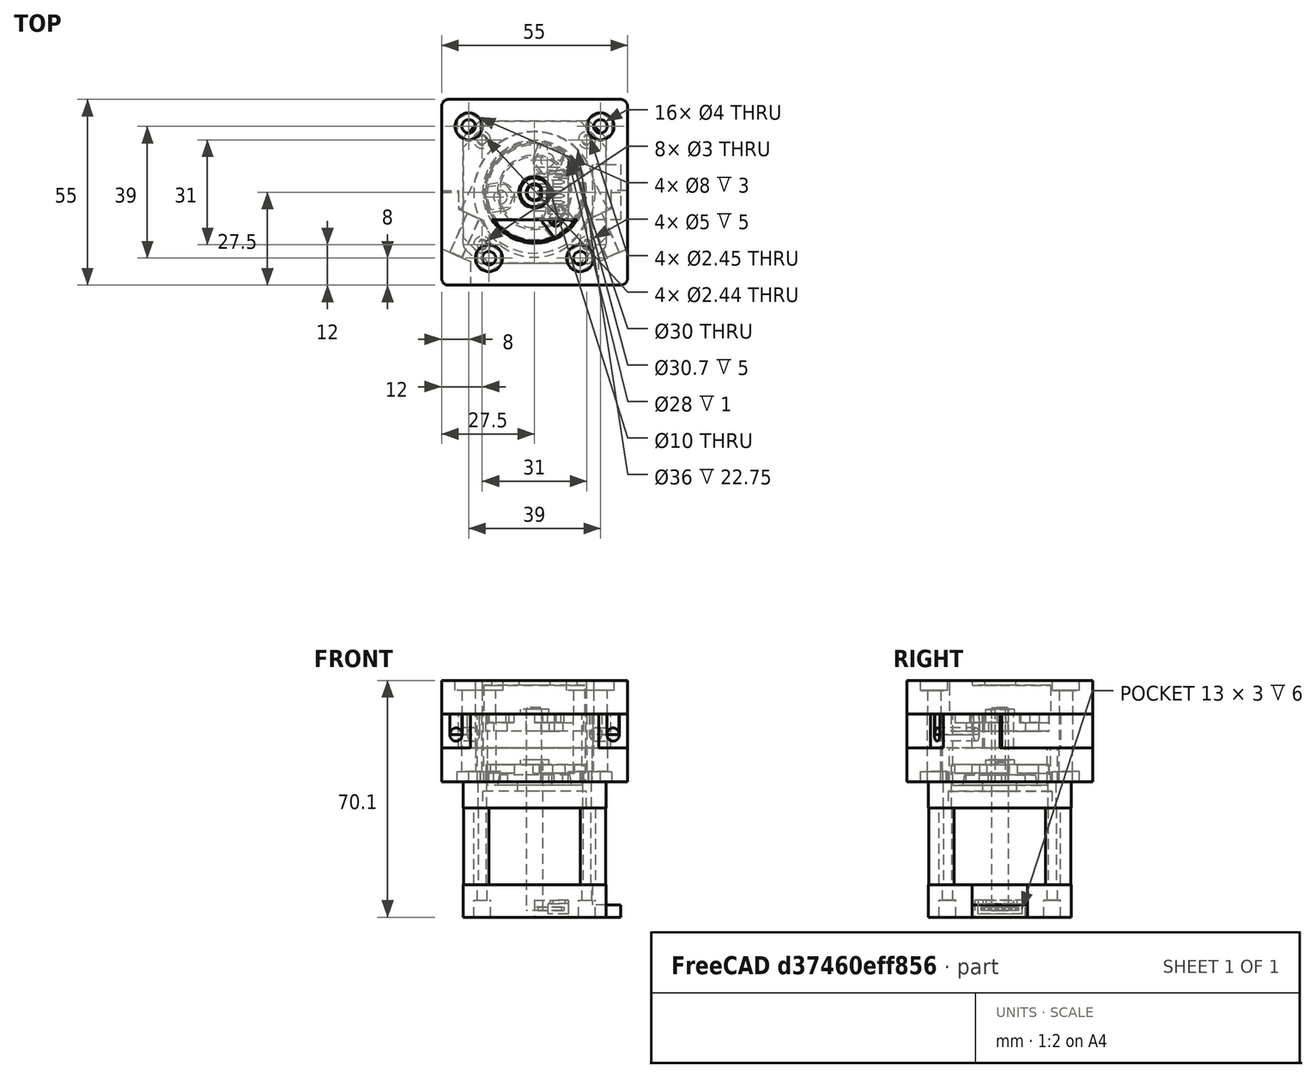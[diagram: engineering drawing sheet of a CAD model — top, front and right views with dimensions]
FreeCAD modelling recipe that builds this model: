
FCSTD DOCUMENT  (FreeCAD 0.19R24291 (Git))
Label: peristaltic-pump
License: All rights reserved
LicenseURL: http://en.wikipedia.org/wiki/All_rights_reserved
objects: Sketcher::SketchObject×44, PartDesign::Pocket×25, PartDesign::Pad×18, PartDesign::Body×12, App::Part×9, Mesh::Feature×5, PartDesign::Chamfer×4, Part::FeaturePython×4, PartDesign::Fillet×2, PartDesign::Mirrored×2, PartDesign::PolarPattern×2, PartDesign::Draft×1, PartDesign::Hole×1, PartDesign::LinearPattern×1, Spreadsheet::Sheet×1, App::MeasureDistance×1
note: 167 computed .brp shape members not serialized (recipe doc carries the construction recipe); baked Part::Feature solids carry a one-line shape summary decoded from their .brp

FEATURE [Sketcher::SketchObject] Sketch
  FullyConstrained = false
  MapMode = 5
  Support = -> [XY_Plane001]
  sketch-geometry (4):
    g0: LineSegment StartX=-21.15 StartY=21.15 StartZ=0 EndX=21.15 EndY=21.15 EndZ=0
    g1: LineSegment StartX=21.15 StartY=21.15 StartZ=0 EndX=21.15 EndY=-21.15 EndZ=0
    g2: LineSegment StartX=21.15 StartY=-21.15 StartZ=0 EndX=-21.15 EndY=-21.15 EndZ=0
    g3: LineSegment StartX=-21.15 StartY=-21.15 StartZ=0 EndX=-21.15 EndY=21.15 EndZ=0
  constraints (11):
    c: Coincident(g0,g1)
    c: Coincident(g1,g2)
    c: Coincident(g2,g3)
    c: Coincident(g3,g0)
    c: Horizontal(g0)
    c: Horizontal(g2)
    c: Vertical(g1)
    c: Vertical(g3)
    c: Symmetric(g0,g1,g-1)
    c: DistanceX(g0,g0) = 42.3
    c: Equal(g0,g3)
FEATURE [PartDesign::Pad] Pad
  AllowMultiFace = false
  Direction = (1,1,1)
  Length = 9.6
  Length2 = 100
  Profile = -> Sketch
  Refine = true
  Type = 0
FEATURE [Sketcher::SketchObject] Sketch001
  ExternalGeometry = -> [Pad]
  FullyConstrained = false
  MapMode = 5
  Support = -> [XY_Plane001]
  sketch-geometry (4):
    g0: LineSegment StartX=21.15 StartY=8.2 StartZ=0 EndX=25.45 EndY=8.2 EndZ=0
    g1: LineSegment StartX=25.45 StartY=8.2 StartZ=0 EndX=25.45 EndY=-8.2 EndZ=0
    g2: LineSegment StartX=25.45 StartY=-8.2 StartZ=0 EndX=21.15 EndY=-8.2 EndZ=0
    g3: LineSegment StartX=21.15 StartY=-8.2 StartZ=0 EndX=21.15 EndY=8.2 EndZ=0
  constraints (11):
    c: Coincident(g0,g1)
    c: Coincident(g1,g2)
    c: Coincident(g2,g3)
    c: Coincident(g3,g0)
    c: Horizontal(g0)
    c: Horizontal(g2)
    c: Vertical(g3)
    c: PointOnObject(g0,g-3)
    c: Symmetric(g1,g0,g-1)
    c: DistanceX(g0,g0) = 4.3
    c: DistanceY(g1,g1) = 16.4
FEATURE [PartDesign::Pad] Pad001
  AllowMultiFace = false
  BaseFeature = -> Pad
  Direction = (1,1,1)
  Length = 3.6
  Length2 = 100
  Profile = -> Sketch001
  Refine = true
  Type = 0
FEATURE [PartDesign::Chamfer] Chamfer
  Angle = 45
  Base = -> Pad001 [Edge13,Edge5,Edge1,Edge2]
  BaseFeature = -> Pad001
  ChamferType = 0
  FlipDirection = false
  Size = 5
  Size2 = 1
  SupportTransform = false
FEATURE [PartDesign::Fillet] Fillet
  Base = -> Chamfer [Edge33,Edge28,Edge18,Edge3,Edge2,Edge16,Edge30,Edge25]
  BaseFeature = -> Chamfer
  Radius = 2
  SupportTransform = false
FEATURE [Sketcher::SketchObject] Sketch002
  FullyConstrained = false
  MapMode = 5
  Support = -> [XY_Plane002]
  sketch-geometry (4):
    g0: LineSegment StartX=-21 StartY=21 StartZ=0 EndX=21 EndY=21 EndZ=0
    g1: LineSegment StartX=21 StartY=21 StartZ=0 EndX=21 EndY=-21 EndZ=0
    g2: LineSegment StartX=21 StartY=-21 StartZ=0 EndX=-21 EndY=-21 EndZ=0
    g3: LineSegment StartX=-21 StartY=-21 StartZ=0 EndX=-21 EndY=21 EndZ=0
  constraints (11):
    c: Coincident(g0,g1)
    c: Coincident(g1,g2)
    c: Coincident(g2,g3)
    c: Coincident(g3,g0)
    c: Horizontal(g0)
    c: Horizontal(g2)
    c: Vertical(g1)
    c: Vertical(g3)
    c: DistanceX(g0,g0) = 42
    c: Symmetric(g0,g1,g-1)
    c: Equal(g0,g3)
FEATURE [PartDesign::Pad] Pad002
  AllowMultiFace = false
  Direction = (1,1,1)
  Length = 22.75
  Length2 = 100
  Profile = -> Sketch002
  Refine = true
  Type = 0
FEATURE [PartDesign::Chamfer] Chamfer001
  Angle = 45
  Base = -> Pad002 [Edge8,Edge1,Edge5,Edge2]
  BaseFeature = -> Pad002
  ChamferType = 0
  FlipDirection = false
  Size = 7.5
  Size2 = 1
  SupportTransform = false
FEATURE [Sketcher::SketchObject] Sketch003
  FullyConstrained = false
  MapMode = 5
  Support = -> [XY_Plane003]
  sketch-geometry (4):
    g0: LineSegment StartX=-21.15 StartY=21.15 StartZ=0 EndX=21.15 EndY=21.15 EndZ=0
    g1: LineSegment StartX=21.15 StartY=21.15 StartZ=0 EndX=21.15 EndY=-21.15 EndZ=0
    g2: LineSegment StartX=21.15 StartY=-21.15 StartZ=0 EndX=-21.15 EndY=-21.15 EndZ=0
    g3: LineSegment StartX=-21.15 StartY=-21.15 StartZ=0 EndX=-21.15 EndY=21.15 EndZ=0
  constraints (11):
    c: Coincident(g0,g1)
    c: Coincident(g1,g2)
    c: Coincident(g2,g3)
    c: Coincident(g3,g0)
    c: Horizontal(g0)
    c: Horizontal(g2)
    c: Vertical(g1)
    c: Vertical(g3)
    c: Symmetric(g0,g1,g-1)
    c: DistanceX(g0,g0) = 42.3
    c: Equal(g0,g3)
FEATURE [PartDesign::Pad] Pad003
  AllowMultiFace = false
  Direction = (1,1,1)
  Length = 7.75
  Length2 = 100
  Profile = -> Sketch003
  Refine = true
  Type = 0
FEATURE [PartDesign::Chamfer] Chamfer002
  Angle = 45
  Base = -> Pad003 [Edge8,Edge5,Edge2,Edge1]
  BaseFeature = -> Pad003
  ChamferType = 0
  FlipDirection = false
  Size = 5
  Size2 = 1
  SupportTransform = false
FEATURE [PartDesign::Fillet] Fillet001
  Base = -> Chamfer002 [Edge22,Edge24,Edge23,Edge21,Edge12,Edge2,Edge3,Edge14]
  BaseFeature = -> Chamfer002
  Radius = 2
  SupportTransform = false
FEATURE [Sketcher::SketchObject] Sketch004
  FullyConstrained = false
  MapMode = 5
  Placement = pos=(0,0,0) rot=(1,0,0;3.14159rad)
  Support = -> [Fillet]
  sketch-geometry (8):
    g0: LineSegment StartX=-15.5 StartY=15.5 StartZ=0 EndX=15.5 EndY=15.5 EndZ=0
    g1: LineSegment StartX=15.5 StartY=15.5 StartZ=0 EndX=15.5 EndY=-15.5 EndZ=0
    g2: LineSegment StartX=15.5 StartY=-15.5 StartZ=0 EndX=-15.5 EndY=-15.5 EndZ=0
    g3: LineSegment StartX=-15.5 StartY=-15.5 StartZ=0 EndX=-15.5 EndY=15.5 EndZ=0
    g4: Circle CenterX=-15.5 CenterY=15.5 CenterZ=0 NormalX=0 NormalY=0 NormalZ=1 AngleXU=0 Radius=1.225
    g5: Circle CenterX=15.5 CenterY=15.5 CenterZ=0 NormalX=0 NormalY=0 NormalZ=1 AngleXU=0 Radius=1.225
    g6: Circle CenterX=15.5 CenterY=-15.5 CenterZ=0 NormalX=0 NormalY=0 NormalZ=1 AngleXU=0 Radius=1.225
    g7: Circle CenterX=-15.5 CenterY=-15.5 CenterZ=0 NormalX=0 NormalY=0 NormalZ=1 AngleXU=0 Radius=1.225
  constraints (19):
    c: Coincident(g0,g1)
    c: Coincident(g1,g2)
    c: Coincident(g2,g3)
    c: Coincident(g3,g0)
    c: Horizontal(g0)
    c: Horizontal(g2)
    c: Vertical(g1)
    c: Vertical(g3)
    c: Symmetric(g0,g1,g-1)
    c: DistanceX(g0,g0) = 31
    c: Equal(g3,g0)
    c: Coincident(g4,g0)
    c: Coincident(g5,g0)
    c: Coincident(g6,g1)
    c: Coincident(g7,g2)
    c: Equal(g6,g5)
    c: Equal(g5,g4)
    c: Equal(g4,g7)
    c: Radius(g4) = 1.225
FEATURE [Sketcher::SketchObject] Sketch005
  FullyConstrained = false
  MapMode = 5
  Placement = pos=(0,0,0) rot=(1,0,0;3.14159rad)
  Support = -> [Chamfer001]
  sketch-geometry (8):
    g0: LineSegment StartX=-15.5 StartY=15.5 StartZ=0 EndX=15.5 EndY=15.5 EndZ=0
    g1: LineSegment StartX=15.5 StartY=15.5 StartZ=0 EndX=15.5 EndY=-15.5 EndZ=0
    g2: LineSegment StartX=15.5 StartY=-15.5 StartZ=0 EndX=-15.5 EndY=-15.5 EndZ=0
    g3: LineSegment StartX=-15.5 StartY=-15.5 StartZ=0 EndX=-15.5 EndY=15.5 EndZ=0
    g4: Circle CenterX=-15.5 CenterY=15.5 CenterZ=0 NormalX=0 NormalY=0 NormalZ=1 AngleXU=0 Radius=1.22
    g5: Circle CenterX=15.5 CenterY=15.5 CenterZ=0 NormalX=0 NormalY=0 NormalZ=1 AngleXU=0 Radius=1.22
    g6: Circle CenterX=15.5 CenterY=-15.5 CenterZ=0 NormalX=0 NormalY=0 NormalZ=1 AngleXU=0 Radius=1.22
    g7: Circle CenterX=-15.5 CenterY=-15.5 CenterZ=0 NormalX=0 NormalY=0 NormalZ=1 AngleXU=0 Radius=1.22
  constraints (19):
    c: Coincident(g0,g1)
    c: Coincident(g1,g2)
    c: Coincident(g2,g3)
    c: Coincident(g3,g0)
    c: Horizontal(g0)
    c: Horizontal(g2)
    c: Vertical(g1)
    c: Vertical(g3)
    c: Equal(g0,g3)
    c: Symmetric(g0,g1,g-1)
    c: DistanceX(g0,g0) = 31
    c: Coincident(g4,g0)
    c: Coincident(g5,g0)
    c: Coincident(g6,g1)
    c: Coincident(g7,g2)
    c: Equal(g6,g5)
    c: Equal(g5,g4)
    c: Equal(g4,g7)
    c: Radius(g4) = 1.22
FEATURE [PartDesign::Pocket] Pocket001
  AllowMultiFace = false
  BaseFeature = -> Chamfer001
  Length = 5
  Length2 = 100
  Profile = -> Sketch005
  Refine = true
  Type = 1
FEATURE [Sketcher::SketchObject] Sketch010
  FullyConstrained = false
  MapMode = 5
  Support = -> [XY_Plane004]
  sketch-geometry (1):
    g0: Circle CenterX=0 CenterY=0 CenterZ=0 NormalX=0 NormalY=0 NormalZ=1 AngleXU=0 Radius=2.5
  constraints (2):
    c: Coincident(g0,g-1)
    c: Radius(g0) = 2.5
FEATURE [PartDesign::Pad] Pad005
  AllowMultiFace = false
  Direction = (1,1,1)
  Length = 60
  Length2 = 100
  Profile = -> Sketch010
  Refine = true
  Type = 0
FEATURE [Sketcher::SketchObject] Sketch011
  FullyConstrained = false
  MapMode = 5
  Placement = pos=(0,0,60) rot=(0,0,1;0rad)
  Support = -> [Pad005]
  sketch-geometry (4):
    g0: LineSegment StartX=2 StartY=2 StartZ=0 EndX=6 EndY=2 EndZ=0
    g1: LineSegment StartX=6 StartY=2 StartZ=0 EndX=6 EndY=-2 EndZ=0
    g2: LineSegment StartX=6 StartY=-2 StartZ=0 EndX=2 EndY=-2 EndZ=0
    g3: LineSegment StartX=2 StartY=-2 StartZ=0 EndX=2 EndY=2 EndZ=0
  constraints (11):
    c: Coincident(g0,g1)
    c: Coincident(g1,g2)
    c: Coincident(g2,g3)
    c: Coincident(g3,g0)
    c: Horizontal(g0)
    c: Horizontal(g2)
    c: Vertical(g1)
    c: Symmetric(g2,g0,g-1)
    c: DistanceX(g-1,g0) = 2
    c: Equal(g0,g3)
    c: DistanceX(g0,g0) = 4
FEATURE [PartDesign::Pocket] Pocket005
  AllowMultiFace = false
  BaseFeature = -> Pad005
  Length = 16
  Length2 = 100
  Profile = -> Sketch011
  Refine = true
  Type = 0
FEATURE [PartDesign::Chamfer] Chamfer003
  Angle = 45
  Base = -> Pocket005 [Edge3,Edge5,Edge9]
  BaseFeature = -> Pocket005
  ChamferType = 0
  FlipDirection = false
  Size = 0.3
  Size2 = 1
  SupportTransform = false
FEATURE [PartDesign::Body] Body003  label="Rotor"
  Group = -> [Sketch010,Pad005,Sketch011,Pocket005,Chamfer003]
  Origin = -> Origin004
  Placement = pos=(0,0,2) rot=(0,0,1;0rad)
  Tip = -> Chamfer003
FEATURE [Sketcher::SketchObject] Sketch012
  FullyConstrained = false
  MapMode = 5
  Placement = pos=(0,0,22.75) rot=(0,0,1;0rad)
  Support = -> [Pocket001]
  sketch-geometry (1):
    g0: Circle CenterX=0 CenterY=0 CenterZ=0 NormalX=0 NormalY=0 NormalZ=1 AngleXU=0 Radius=18
  constraints (2):
    c: Coincident(g0,g-1)
    c: Radius(g0) = 18
FEATURE [Sketcher::SketchObject] Sketch006
  FullyConstrained = false
  MapMode = 5
  Placement = pos=(0,0,7.75) rot=(0,0,1;0rad)
  Support = -> [Fillet001]
  sketch-geometry (8):
    g0: LineSegment StartX=-15.5 StartY=15.5 StartZ=0 EndX=15.5 EndY=15.5 EndZ=0
    g1: LineSegment StartX=15.5 StartY=15.5 StartZ=0 EndX=15.5 EndY=-15.5 EndZ=0
    g2: LineSegment StartX=15.5 StartY=-15.5 StartZ=0 EndX=-15.5 EndY=-15.5 EndZ=0
    g3: LineSegment StartX=-15.5 StartY=-15.5 StartZ=0 EndX=-15.5 EndY=15.5 EndZ=0
    g4: Circle CenterX=-15.5 CenterY=15.5 CenterZ=0 NormalX=0 NormalY=0 NormalZ=1 AngleXU=0 Radius=1.225
    g5: Circle CenterX=15.5 CenterY=15.5 CenterZ=0 NormalX=0 NormalY=0 NormalZ=1 AngleXU=0 Radius=1.225
    g6: Circle CenterX=15.5 CenterY=-15.5 CenterZ=0 NormalX=0 NormalY=0 NormalZ=1 AngleXU=0 Radius=1.225
    g7: Circle CenterX=-15.5 CenterY=-15.5 CenterZ=0 NormalX=0 NormalY=0 NormalZ=1 AngleXU=0 Radius=1.225
  constraints (19):
    c: Coincident(g0,g1)
    c: Coincident(g1,g2)
    c: Coincident(g2,g3)
    c: Coincident(g3,g0)
    c: Horizontal(g0)
    c: Horizontal(g2)
    c: Vertical(g1)
    c: Vertical(g3)
    c: Equal(g0,g3)
    c: Symmetric(g0,g1,g-1)
    c: DistanceX(g0,g0) = 31
    c: Coincident(g4,g0)
    c: Coincident(g7,g2)
    c: Coincident(g0,g5)
    c: Coincident(g1,g6)
    c: Equal(g7,g4)
    c: Equal(g4,g5)
    c: Equal(g5,g6)
    c: Radius(g4) = 1.225
FEATURE [PartDesign::Pocket] Pocket002
  AllowMultiFace = false
  BaseFeature = -> Fillet001
  Length = 5
  Length2 = 100
  Profile = -> Sketch006
  Refine = true
  Type = 1
FEATURE [Sketcher::SketchObject] Sketch007
  FullyConstrained = false
  MapMode = 5
  Placement = pos=(0,0,7.75) rot=(0,0,1;0rad)
  Support = -> [Pocket002]
  sketch-geometry (1):
    g0: Circle CenterX=0 CenterY=0 CenterZ=0 NormalX=0 NormalY=0 NormalZ=1 AngleXU=0 Radius=14
  constraints (2):
    c: Coincident(g0,g-1)
    c: Radius(g0) = 14
FEATURE [PartDesign::Pocket] Pocket003
  AllowMultiFace = false
  BaseFeature = -> Pocket002
  Length = 1
  Length2 = 100
  Profile = -> Sketch007
  Refine = true
  Type = 0
FEATURE [Sketcher::SketchObject] Sketch008
  FullyConstrained = false
  MapMode = 5
  Placement = pos=(0,0,6.75) rot=(0,0,1;0rad)
  Support = -> [Pocket003]
  sketch-geometry (1):
    g0: Circle CenterX=0 CenterY=0 CenterZ=0 NormalX=0 NormalY=0 NormalZ=1 AngleXU=0 Radius=11
  constraints (2):
    c: Coincident(g0,g-1)
    c: Radius(g0) = 11
FEATURE [PartDesign::Pad] Pad004
  AllowMultiFace = false
  BaseFeature = -> Pocket003
  Direction = (1,1,1)
  Length = 3
  Length2 = 100
  Profile = -> Sketch008
  Refine = true
  Type = 0
FEATURE [PartDesign::Draft] Draft
  Angle = 10
  Base = -> Pad004 [Face25]
  BaseFeature = -> Pad004
  NeutralPlane = -> Pad004 [Face24]
  SupportTransform = false
FEATURE [Sketcher::SketchObject] Sketch009
  FullyConstrained = false
  MapMode = 5
  Placement = pos=(0,0,9.75) rot=(0,0,1;0rad)
  Support = -> [Draft]
  sketch-geometry (1):
    g0: Circle CenterX=0 CenterY=0 CenterZ=0 NormalX=0 NormalY=0 NormalZ=1 AngleXU=0 Radius=5
  constraints (2):
    c: Coincident(g0,g-1)
    c: Radius(g0) = 5
FEATURE [PartDesign::Pocket] Pocket004
  AllowMultiFace = false
  BaseFeature = -> Draft
  Length = 8
  Length2 = 100
  Profile = -> Sketch009
  Refine = true
  Type = 1
FEATURE [PartDesign::Hole] Hole
  AllowMultiFace = false
  BaseFeature = -> Fillet
  Depth = 25
  DepthType = 0
  Diameter = 3
  DrillForDepth = false
  DrillPoint = 1
  DrillPointAngle = 118
  HoleCutCountersinkAngle = 90
  HoleCutCustomValues = false
  HoleCutDepth = 5
  HoleCutDiameter = 5
  HoleCutType = 1
  ModelActualThread = false
  Profile = -> Sketch004
  Refine = true
  Tapered = false
  TaperedAngle = 90
  ThreadAngle = 0
  ThreadClass = 0
  ThreadCutOffInner = 0
  ThreadCutOffOuter = 0
  ThreadDirection = 0
  ThreadFit = 0
  ThreadPitch = 0
  ThreadSize = 0
  ThreadType = 0
  Threaded = false
FEATURE [Part::FeaturePython] Screw  label="M2.5x25-Screw"  # Fasteners workbench fastener (typed FeaturePython)
  Placement = pos=(15.5,15.5,4) rot=(0,1,0;3.14159rad)
  diameter = 3
  invert = true
  length = 10
  matchOuter = true
  offset = 1
  thread = true
  type = 16
FEATURE [Part::FeaturePython] Screw001  label="M2.5x25-Screw006"  # Fasteners workbench fastener (typed FeaturePython)
  Placement = pos=(-15.5,-15.5,4) rot=(0,1,0;3.14159rad)
  diameter = 3
  invert = true
  length = 10
  matchOuter = true
  offset = 1
  thread = true
  type = 16
FEATURE [Part::FeaturePython] Screw002  label="M2.5x25-Screw005"  # Fasteners workbench fastener (typed FeaturePython)
  Placement = pos=(15.5,-15.5,4) rot=(0,1,0;3.14159rad)
  diameter = 3
  invert = true
  length = 10
  matchOuter = true
  offset = 1
  thread = true
  type = 16
FEATURE [Part::FeaturePython] Screw003  label="M2.5x25-Screw007"  # Fasteners workbench fastener (typed FeaturePython)
  Placement = pos=(-15.5,15.5,4) rot=(0,1,0;3.14159rad)
  diameter = 3
  invert = true
  length = 10
  matchOuter = true
  offset = 1
  thread = true
  type = 16
FEATURE [App::Part] Part004  label="Rotor001"
  Group = -> [Body003]
  Origin = -> Origin008
FEATURE [App::Part] Part005  label="Screw"
  Group = -> [Screw,Screw001,Screw002,Screw003]
  Origin = -> Origin009
FEATURE [PartDesign::Body] Body004  label="Stator"
  Origin = -> Origin010
FEATURE [PartDesign::Pocket] Pocket
  AllowMultiFace = false
  BaseFeature = -> Pocket001
  Length = 5
  Length2 = 100
  Profile = -> Sketch012
  Refine = true
  Type = 1
FEATURE [PartDesign::Body] Body001
  Group = -> [Sketch002,Pad002,Chamfer001,Sketch005,Pocket001,Sketch012,Pocket]
  Origin = -> Origin002
  Placement = pos=(0,0,9.6) rot=(0,0,1;0rad)
  Tip = -> Pocket
FEATURE [App::Part] Part002  label="Body"
  Group = -> [Body001,Body004]
  Origin = -> Origin006
FEATURE [Sketcher::SketchObject] Sketch013
  ExternalGeometry = -> [Hole]
  FullyConstrained = false
  MapMode = 5
  Placement = pos=(21.15,0,0) rot=(0.57735,0.57735,0.57735;2.0944rad)
  Support = -> [Hole]
  sketch-geometry (4):
    g0: LineSegment StartX=-8.2 StartY=3.6 StartZ=0 EndX=8.2 EndY=3.6 EndZ=0
    g1: LineSegment StartX=8.2 StartY=3.6 StartZ=0 EndX=8.2 EndY=9.6 EndZ=0
    g2: LineSegment StartX=8.2 StartY=9.6 StartZ=0 EndX=-8.2 EndY=9.6 EndZ=0
    g3: LineSegment StartX=-8.2 StartY=9.6 StartZ=0 EndX=-8.2 EndY=3.6 EndZ=0
  constraints (10):
    c: Coincident(g0,g1)
    c: Coincident(g1,g2)
    c: Coincident(g2,g3)
    c: Coincident(g3,g0)
    c: Horizontal(g0)
    c: Vertical(g1)
    c: Vertical(g3)
    c: Coincident(g0,g-3)
    c: PointOnObject(g1,g-5)
    c: Symmetric(g2,g1,g-2)
FEATURE [PartDesign::Pocket] Pocket006
  AllowMultiFace = false
  BaseFeature = -> Hole
  Length = 4
  Length2 = 100
  Profile = -> Sketch013
  Refine = true
  Type = 0
FEATURE [PartDesign::Body] Body  label="Aluminium rear001"
  Group = -> [Sketch,Pad,Sketch001,Pad001,Chamfer,Fillet,Sketch004,Hole,Sketch013,Pocket006]
  Origin = -> Origin001
  Tip = -> Pocket006
FEATURE [App::Part] Part001  label="Aluminium rear"
  Group = -> [Body]
  Origin = -> Origin005
FEATURE [Sketcher::SketchObject] Sketch014
  FullyConstrained = false
  MapMode = 5
  Placement = pos=(0,0,0) rot=(0.57735,0.57735,0.57735;2.0944rad)
  Support = -> [YZ_Plane012]
  sketch-geometry (4):
    g0: LineSegment StartX=-7.5 StartY=0 StartZ=0 EndX=7.5 EndY=0 EndZ=0
    g1: LineSegment StartX=7.5 StartY=0 StartZ=0 EndX=7.5 EndY=5 EndZ=0
    g2: LineSegment StartX=7.5 StartY=5 StartZ=0 EndX=-7.5 EndY=5 EndZ=0
    g3: LineSegment StartX=-7.5 StartY=5 StartZ=0 EndX=-7.5 EndY=0 EndZ=0
  constraints (11):
    c: Coincident(g0,g1)
    c: Coincident(g1,g2)
    c: Coincident(g2,g3)
    c: Coincident(g3,g0)
    c: Horizontal(g0)
    c: Horizontal(g2)
    c: Vertical(g1)
    c: Vertical(g3)
    c: Symmetric(g0,g0,g-1)
    c: DistanceX(g0,g0) = 15
    c: DistanceY(g3,g3) = 5
FEATURE [PartDesign::Pad] Pad006
  AllowMultiFace = false
  Direction = (1,1,1)
  Length = 10
  Length2 = 100
  Placement = pos=(0,0,0) rot=(0.57735,0.57735,0.57735;2.0944rad)
  Profile = -> Sketch014
  Refine = true
  Type = 0
FEATURE [Sketcher::SketchObject] Sketch015
  ExternalGeometry = -> [Pad006]
  FullyConstrained = false
  MapMode = 5
  Placement = pos=(10,-2.2e-15,2.2e-15) rot=(0.57735,0.57735,0.57735;2.0944rad)
  Support = -> [Pad006]
  sketch-geometry (8):
    g0: LineSegment StartX=-6.5 StartY=4 StartZ=0 EndX=6.5 EndY=4 EndZ=0
    g1: LineSegment StartX=6.5 StartY=4 StartZ=0 EndX=6.5 EndY=1 EndZ=0
    g2: LineSegment StartX=6.5 StartY=1 StartZ=0 EndX=-6.5 EndY=1 EndZ=0
    g3: LineSegment StartX=-6.5 StartY=1 StartZ=0 EndX=-6.5 EndY=4 EndZ=0
    g4: LineSegment StartX=-6.5 StartY=1 StartZ=0 EndX=-7.5 EndY=1 EndZ=0
    g5: LineSegment StartX=-6.5 StartY=1 StartZ=0 EndX=-6.5 EndY=0 EndZ=0
    g6: LineSegment StartX=6.5 StartY=4 StartZ=0 EndX=6.5 EndY=5 EndZ=0
    g7: LineSegment StartX=6.5 StartY=4 StartZ=0 EndX=7.5 EndY=4 EndZ=0
  constraints (23):
    c: Coincident(g0,g1)
    c: Coincident(g1,g2)
    c: Coincident(g2,g3)
    c: Coincident(g3,g0)
    c: Horizontal(g2)
    c: Vertical(g1)
    c: Vertical(g3)
    c: Symmetric(g0,g0,g-2)
    c: Coincident(g4,g2)
    c: PointOnObject(g4,g-4)
    c: Horizontal(g4)
    c: PointOnObject(g5,g-1)
    c: Vertical(g5)
    c: Coincident(g6,g0)
    c: Coincident(g7,g0)
    c: Horizontal(g7)
    c: Vertical(g6)
    c: PointOnObject(g6,g-5)
    c: Equal(g7,g6)
    c: Equal(g6,g4)
    c: Equal(g4,g5)
    c: DistanceX(g4,g4) = 1
    c: Coincident(g5,g2)
FEATURE [PartDesign::Pocket] Pocket007
  AllowMultiFace = false
  BaseFeature = -> Pad006
  Length = 6
  Length2 = 100
  Placement = pos=(0,0,0) rot=(0.57735,0.57735,0.57735;2.0944rad)
  Profile = -> Sketch015
  Refine = true
  Type = 0
FEATURE [Sketcher::SketchObject] Sketch016
  ExternalGeometry = -> [Pocket007]
  FullyConstrained = false
  MapMode = 5
  Placement = pos=(10,-2.2e-15,2.2e-15) rot=(0.57735,0.57735,0.57735;2.0944rad)
  Support = -> [Pocket007]
  sketch-geometry (4):
    g0: LineSegment StartX=-4 StartY=5 StartZ=0 EndX=4 EndY=5 EndZ=0
    g1: LineSegment StartX=4 StartY=5 StartZ=0 EndX=4 EndY=4 EndZ=0
    g2: LineSegment StartX=4 StartY=4 StartZ=0 EndX=-4 EndY=4 EndZ=0
    g3: LineSegment StartX=-4 StartY=4 StartZ=0 EndX=-4 EndY=5 EndZ=0
  constraints (11):
    c: Coincident(g0,g1)
    c: Coincident(g1,g2)
    c: Coincident(g2,g3)
    c: Coincident(g3,g0)
    c: Horizontal(g0)
    c: Vertical(g1)
    c: Vertical(g3)
    c: PointOnObject(g0,g-3)
    c: PointOnObject(g1,g-4)
    c: Symmetric(g1,g2,g-2)
    c: DistanceX(g0,g0) = 8
FEATURE [PartDesign::Pocket] Pocket008
  AllowMultiFace = false
  BaseFeature = -> Pocket007
  Length = 4.5
  Length2 = 100
  Placement = pos=(0,0,0) rot=(0.57735,0.57735,0.57735;2.0944rad)
  Profile = -> Sketch016
  Refine = true
  Type = 0
FEATURE [Sketcher::SketchObject] Sketch017
  ExternalGeometry = -> [Pocket008]
  FullyConstrained = false
  MapMode = 5
  Placement = pos=(-1.4e-15,2.2e-15,5) rot=(0,0,-1;1.5708rad)
  Support = -> [Pocket008]
  sketch-geometry (11):
    g0: LineSegment StartX=-6.49 StartY=8.99 StartZ=0 EndX=-5.01 EndY=8.99 EndZ=0
    g1: LineSegment StartX=-5.01 StartY=8.99 StartZ=0 EndX=-5.01 EndY=4.5 EndZ=0
    g2: LineSegment StartX=-5.01 StartY=4.5 StartZ=0 EndX=-6.49 EndY=4.5 EndZ=0
    g3: LineSegment StartX=-6.49 StartY=4.5 StartZ=0 EndX=-6.49 EndY=8.99 EndZ=0
    g4: LineSegment StartX=5.01 StartY=8.99 StartZ=0 EndX=6.49 EndY=8.99 EndZ=0
    g5: LineSegment StartX=6.49 StartY=8.99 StartZ=0 EndX=6.49 EndY=4.5 EndZ=0
    g6: LineSegment StartX=6.49 StartY=4.5 StartZ=0 EndX=5.01 EndY=4.5 EndZ=0
    g7: LineSegment StartX=5.01 StartY=4.5 StartZ=0 EndX=5.01 EndY=8.99 EndZ=0
    g8: LineSegment StartX=-7.5 StartY=8.99 StartZ=0 EndX=-6.49 EndY=8.99 EndZ=0
    g9: LineSegment StartX=-6.49 StartY=10 StartZ=0 EndX=-6.49 EndY=8.99 EndZ=0
    g10: LineSegment StartX=-5.01 StartY=8.99 StartZ=0 EndX=-4 EndY=8.99 EndZ=0
  constraints (32):
    c: Coincident(g0,g1)
    c: Coincident(g1,g2)
    c: Coincident(g2,g3)
    c: Coincident(g3,g0)
    c: Horizontal(g0)
    c: Horizontal(g2)
    c: Vertical(g1)
    c: Vertical(g3)
    c: Coincident(g4,g5)
    c: Coincident(g5,g6)
    c: Coincident(g6,g7)
    c: Coincident(g7,g4)
    c: Horizontal(g4)
    c: Horizontal(g6)
    c: Vertical(g5)
    c: Vertical(g7)
    c: DistanceX(g4,g4) = 1.48
    c: Equal(g0,g4)
    c: Equal(g7,g1)
    c: PointOnObject(g8,g-4)
    c: Coincident(g8,g0)
    c: Horizontal(g8)
    c: PointOnObject(g9,g-5)
    c: Coincident(g9,g0)
    c: Vertical(g9)
    c: Coincident(g10,g0)
    c: PointOnObject(g10,g-3)
    c: Horizontal(g10)
    c: Symmetric(g4,g0,g-2)
    c: Equal(g10,g9)
    c: Equal(g9,g8)
    c: DistanceY(g3,g3) = 4.49
FEATURE [PartDesign::Pocket] Pocket009
  AllowMultiFace = false
  BaseFeature = -> Pocket008
  Length = 2
  Length2 = 100
  Placement = pos=(0,0,0) rot=(0.57735,0.57735,0.57735;2.0944rad)
  Profile = -> Sketch017
  Refine = true
  Type = 0
FEATURE [PartDesign::Body] Body005  label="conector"
  Group = -> [Sketch014,Pad006,Sketch015,Pocket007,Sketch016,Pocket008,Sketch017,Pocket009]
  Origin = -> Origin012
  Tip = -> Pocket009
FEATURE [Sketcher::SketchObject] Sketch018
  FullyConstrained = false
  MapMode = 5
  Placement = pos=(0,0,0) rot=(0.57735,0.57735,0.57735;2.0944rad)
  Support = -> [YZ_Plane013]
  sketch-geometry (4):
    g0: LineSegment StartX=-5.5 StartY=1 StartZ=0 EndX=5.5 EndY=1 EndZ=0
    g1: LineSegment StartX=5.5 StartY=1 StartZ=0 EndX=5.5 EndY=0 EndZ=0
    g2: LineSegment StartX=5.5 StartY=0 StartZ=0 EndX=-5.5 EndY=0 EndZ=0
    g3: LineSegment StartX=-5.5 StartY=0 StartZ=0 EndX=-5.5 EndY=1 EndZ=0
  constraints (11):
    c: Coincident(g0,g1)
    c: Coincident(g1,g2)
    c: Coincident(g2,g3)
    c: Coincident(g3,g0)
    c: Horizontal(g0)
    c: Vertical(g1)
    c: Vertical(g3)
    c: PointOnObject(g1,g-1)
    c: DistanceY(g3,g3) = 1
    c: DistanceX(g2,g2) = 11
    c: Symmetric(g1,g2,g-2)
FEATURE [PartDesign::Pad] Pad007
  AllowMultiFace = false
  Direction = (1,1,1)
  Length = 1
  Length2 = 100
  Placement = pos=(0,0,0) rot=(0.57735,0.57735,0.57735;2.0944rad)
  Profile = -> Sketch018
  Refine = true
  Type = 0
FEATURE [Sketcher::SketchObject] Sketch019
  ExternalGeometry = -> [Pad007]
  FullyConstrained = false
  MapMode = 5
  Placement = pos=(-3e-16,4e-16,1) rot=(0,0,-1;1.5708rad)
  Support = -> [Pad007]
  sketch-geometry (7):
    g0: LineSegment StartX=-5.5 StartY=1 StartZ=0 EndX=-4.5 EndY=1 EndZ=0
    g1: LineSegment StartX=-4.5 StartY=1 StartZ=0 EndX=-4.5 EndY=8 EndZ=0
    g2: LineSegment StartX=-4.5 StartY=8 StartZ=0 EndX=-5.5 EndY=8 EndZ=0
    g3: LineSegment StartX=-5.5 StartY=8 StartZ=0 EndX=-5.5 EndY=1 EndZ=0
    g4: LineSegment StartX=-5.5 StartY=8 StartZ=0 EndX=-5.25 EndY=8.7 EndZ=0
    g5: LineSegment StartX=-5.25 StartY=8.7 StartZ=0 EndX=-4.75 EndY=8.7 EndZ=0
    g6: LineSegment StartX=-4.75 StartY=8.7 StartZ=0 EndX=-4.5 EndY=8 EndZ=0
  constraints (19):
    c: Coincident(g0,g1)
    c: Coincident(g1,g2)
    c: Coincident(g2,g3)
    c: Coincident(g3,g0)
    c: Horizontal(g0)
    c: Horizontal(g2)
    c: Vertical(g1)
    c: Vertical(g3)
    c: Coincident(g0,g-3)
    c: Coincident(g2,g4)
    c: Coincident(g4,g5)
    c: Horizontal(g5)
    c: Coincident(g5,g6)
    c: Coincident(g6,g1)
    c: DistanceY(g1,g5) = 0.7
    c: DistanceX(g5,g5) = 0.5
    c: Equal(g6,g4)
    c: DistanceX(g0,g0) = 1
    c: DistanceY(g3,g3) = 7
FEATURE [PartDesign::Pad] Pad008
  AllowMultiFace = false
  BaseFeature = -> Pad007
  Direction = (1,1,1)
  Length = 1
  Length2 = 100
  Placement = pos=(0,0,0) rot=(0.57735,0.57735,0.57735;2.0944rad)
  Profile = -> Sketch019
  Refine = true
  Reversed = true
  Type = 0
FEATURE [PartDesign::LinearPattern] LinearPattern
  BaseFeature = -> Pad008
  Direction = -> Pad008 [Edge10]
  Length = 10
  Occurrences = 6
  Originals = -> [Pad008]
  Placement = pos=(0,0,0) rot=(0.57735,0.57735,0.57735;2.0944rad)
  Refine = true
  Reversed = true
FEATURE [PartDesign::Body] Body006  label="pin"
  Group = -> [Sketch018,Pad007,Sketch019,Pad008,LinearPattern]
  Origin = -> Origin013
  Placement = pos=(0,0,2) rot=(0,0,1;0rad)
  Tip = -> LinearPattern
FEATURE [App::Part] Part006  label="Conector"
  Group = -> [Body005,Body006]
  Origin = -> Origin011
  Placement = pos=(17,0,4) rot=(0,0,1;0rad)
FEATURE [Sketcher::SketchObject] Sketch020
  FullyConstrained = false
  MapMode = 5
  Placement = pos=(0,0,0) rot=(1,0,0;3.14159rad)
  Support = -> [Pocket004]
  sketch-geometry (1):
    g0: Circle CenterX=0 CenterY=0 CenterZ=0 NormalX=0 NormalY=0 NormalZ=1 AngleXU=0 Radius=15.35
  constraints (2):
    c: Coincident(g0,g-1)
    c: Radius(g0) = 15.35
FEATURE [PartDesign::Pocket] Pocket010
  AllowMultiFace = false
  BaseFeature = -> Pocket004
  Length = 5
  Length2 = 100
  Profile = -> Sketch020
  Refine = true
  Type = 0
FEATURE [PartDesign::Body] Body002  label="Aluminum front001"
  Group = -> [Sketch003,Pad003,Chamfer002,Fillet001,Sketch006,Pocket002,Sketch007,Pocket003,Sketch008,Pad004,Draft,Sketch009,Pocket004,Sketch020,Pocket010]
  Origin = -> Origin003
  Placement = pos=(0,0,32.35) rot=(0,0,1;0rad)
  Tip = -> Pocket010
FEATURE [App::Part] Part003  label="Aluminum front"
  Group = -> [Body002]
  Origin = -> Origin007
FEATURE [Spreadsheet::Sheet] Spreadsheet
  cells = A1=variable; B1=value; A2=casing_offset; B2(casing_offset)=40.1; A3=base_width; B3(base_width)=55; A4=base_length; B4(base_length)=55; A5=base_thicc; B5(base_thicc)=10; A6=base_construction_circle_dia; B6(base_construction_circle_dia)=30; A7=tubing_dia; B7(tubing_dia)=4; A8=tube_inlet_port_wall_width; B8(tube_inlet_port_wall_width)=8; A9=upper_mount_holes_dist_to_origin; B9(upper_mount_holes_dist_to_origin)=19.5; A10=lower_mount_holes_dist_to_origin_x; B10(lower_mount_holes_dist_to_origin_x)=13.5; A11=lower_mount_holes_dist_to_origin_y; B11(lower_mount_holes_dist_to_origin_y)==upper_mount_holes_dist_to_origin; A12=mount_holes_dia; B12(mount_holes_dia)=4; A13=lid_thicc; B13(lid_thicc)==base_thicc; A14=bearing_hub_thicc; B14(bearing_hub_thicc)=5; A15=bearing_hub_pad_depth; B15(bearing_hub_pad_depth)=2.5; A16=bearing_hub_dia; B16(bearing_hub_dia)==base_construction_circle_dia - 1; A17=bearing_roller_dist_to_center; B17(bearing_roller_dist_to_center)=10.2; A18=bearing_stp_motor_bevel_dia; B18(bearing_stp_motor_bevel_dia)=8.5; A19=bearing_stp_motor_bevel_height; B19(bearing_stp_motor_bevel_height)=1.5; A20=bearing_stp_motor_spindle_dia; B20(bearing_stp_motor_spindle_dia)=5; A21=bearing_stp_motor_spindle_len; B21(bearing_stp_motor_spindle_len)=3
FEATURE [Mesh::Feature] tube_support  label="tube-support-ralf"
  Placement = pos=(-8.5,24,22) rot=(0,0,1;0rad)
FEATURE [Mesh::Feature] bearing_hub_top  label="bearing-hub-top-ralf"
  Placement = pos=(25.6762,8.58783,33) rot=(0,0,-1;5.61996rad)
FEATURE [Mesh::Feature] pump_top  label="pump-top"
  Placement = pos=(55.5,1.5,49) rot=(0,-1,0;3.14159rad)
FEATURE [Mesh::Feature] bearing_hub  label="bearing-hub-ralf"
  Placement = pos=(13.5,14.5,4) rot=(0,0,1;0rad)
FEATURE [Mesh::Feature] pump_base  label="pump-base"
  Placement = pos=(0.5,1.5,0) rot=(0,0,1;0rad)
FEATURE [App::Part] Part008  label="ralf_overlay"
  Group = -> [tube_support,bearing_hub_top,pump_top,bearing_hub,pump_base]
  Origin = -> Origin015
  Placement = pos=(-28,-29,43) rot=(0,0,1;0rad)
FEATURE [App::MeasureDistance] Distance  label="Distance: 40.10 mm"
  Distance = 40.1
  P1 = (-15.3216,-21.15,40.1)
  P2 = (-15.3216,-21.15,0)
FEATURE [App::Part] Part  label="Nema 17"
  Group = -> [Part001,Part002,Part003,Part004,Part005,Part006,Distance]
  Origin = -> Origin
FEATURE [Sketcher::SketchObject] Sketch021
  AttachmentOffset = pos=(0,0,40.1) rot=(0,0,1;0rad)
  FullyConstrained = true
  MapMode = 5
  Placement = pos=(0,0,40.1) rot=(0,0,1;0rad)
  Support = -> [XY_Plane]
  expr: Constraints[8] = Spreadsheet.base_length
  expr: .AttachmentOffset.Base.z = Spreadsheet.casing_offset
  expr: Constraints[7] = Spreadsheet.base_width
  sketch-geometry (14):
    g0: LineSegment StartX=-25.5 StartY=27.5 StartZ=0 EndX=25.5 EndY=27.5 EndZ=0
    g1: LineSegment StartX=27.5 StartY=25.5 StartZ=0 EndX=27.5 EndY=-25.5 EndZ=0
    g2: LineSegment StartX=25.5 StartY=-27.5 StartZ=0 EndX=-25.5 EndY=-27.5 EndZ=0
    g3: LineSegment StartX=-27.5 StartY=-25.5 StartZ=0 EndX=-27.5 EndY=25.5 EndZ=0
    g4: GeomPoint X=0 Y=27.5 Z=0
    g5: GeomPoint X=27.5 Y=0 Z=0
    g6: ArcOfCircle CenterX=25.5 CenterY=25.5 CenterZ=0 NormalX=0 NormalY=0 NormalZ=1 AngleXU=0 Radius=2 StartAngle=-9e-16 EndAngle=1.5708
    g7: GeomPoint X=27.5 Y=27.5 Z=0
    g8: ArcOfCircle CenterX=-25.5 CenterY=25.5 CenterZ=0 NormalX=0 NormalY=0 NormalZ=1 AngleXU=0 Radius=2 StartAngle=1.5708 EndAngle=3.14159
    g9: GeomPoint X=-27.5 Y=27.5 Z=0
    g10: ArcOfCircle CenterX=25.5 CenterY=-25.5 CenterZ=0 NormalX=0 NormalY=0 NormalZ=1 AngleXU=0 Radius=2 StartAngle=4.71239 EndAngle=6.28319
    g11: GeomPoint X=27.5 Y=-27.5 Z=0
    g12: ArcOfCircle CenterX=-25.5 CenterY=-25.5 CenterZ=0 NormalX=0 NormalY=0 NormalZ=1 AngleXU=0 Radius=2 StartAngle=3.14159 EndAngle=4.71239
    g13: GeomPoint X=-27.5 Y=-27.5 Z=0
  constraints (30):
    c: Horizontal(g0)
    c: Horizontal(g2)
    c: Vertical(g1)
    c: Vertical(g3)
    c: Symmetric(g7,g9,g4)
    c: Symmetric(g7,g11,g5)
    c: PointOnObject(g5,g-1)
    c: DistanceX(g9,g7) = 55
    c: DistanceY(g11,g7) = 55
    c: PointOnObject(g4,g-2)
    c: PointOnObject(g7,g0)
    c: PointOnObject(g7,g1)
    c: Tangent(g0,g6) = 1.5708
    c: Tangent(g1,g6) = 1.5708
    c: PointOnObject(g9,g0)
    c: PointOnObject(g9,g3)
    c: Tangent(g0,g8) = 1.5708
    c: Tangent(g3,g8) = 1.5708
    c: PointOnObject(g11,g1)
    c: PointOnObject(g11,g2)
    c: Tangent(g1,g10) = 1.5708
    c: Tangent(g2,g10) = 1.5708
    c: PointOnObject(g13,g2)
    c: PointOnObject(g13,g3)
    c: Tangent(g2,g12) = 1.5708
    c: Tangent(g3,g12) = 1.5708
    c: Radius(g6) = 2
    c: Equal(g8,g10)
    c: Equal(g10,g12)
    c: Equal(g12,g6)
FEATURE [PartDesign::Pad] Pad009
  Direction = (1,1,1)
  Length = 10
  Length2 = 100
  Profile = -> Sketch021
  Type = 0
  expr: Length = Spreadsheet.base_thicc
FEATURE [Sketcher::SketchObject] Sketch022
  AttachmentOffset = pos=(0,0,50.1) rot=(0,0,1;0rad)
  FullyConstrained = true
  MapMode = 5
  Placement = pos=(0,0,50.1) rot=(0,0,1;0rad)
  Support = -> [XY_Plane016]
  expr: Constraints[29] = Spreadsheet.base_width
  expr: Constraints[36] = Spreadsheet.base_construction_circle_dia + 2
  expr: .AttachmentOffset.Base.z = Spreadsheet.casing_offset + Spreadsheet.base_thicc
  expr: Constraints[39] = Spreadsheet.base_length / 2
  sketch-geometry (19):
    g0: LineSegment StartX=-27.5 StartY=0 StartZ=0 EndX=-22.5 EndY=0 EndZ=0
    g1: LineSegment StartX=-22.5 StartY=0 StartZ=0 EndX=-22.5 EndY=-5 EndZ=0
    g2: LineSegment StartX=-22.5 StartY=-5 StartZ=0 EndX=-15.1966 EndY=-8.26504 EndZ=0
    g3: LineSegment StartX=-27.5 StartY=0 StartZ=0 EndX=-27.5 EndY=-16.7 EndZ=0
    g4: LineSegment StartX=-27.5 StartY=-16.7 StartZ=0 EndX=-19 EndY=-20.5 EndZ=0
    g5: LineSegment StartX=-19 StartY=-20.5 StartZ=0 EndX=-19 EndY=-27.5 EndZ=0
    g6: LineSegment StartX=-19 StartY=-27.5 StartZ=0 EndX=19 EndY=-27.5 EndZ=0
    g7: LineSegment StartX=19 StartY=-27.5 StartZ=0 EndX=19 EndY=-20.5 EndZ=0
    g8: LineSegment StartX=19 StartY=-20.5 StartZ=0 EndX=27.5 EndY=-16.7 EndZ=0
    g9: LineSegment StartX=27.5 StartY=-16.7 StartZ=0 EndX=27.5 EndY=-7.1e-15 EndZ=0
    g10: LineSegment StartX=22.5 StartY=-7.1e-15 StartZ=0 EndX=22.5 EndY=-5 EndZ=0
    g11: LineSegment StartX=22.5 StartY=-5 StartZ=0 EndX=15.1966 EndY=-8.26504 EndZ=0
    g12: ArcOfCircle CenterX=-1e-16 CenterY=-3.25875 CenterZ=0 NormalX=0 NormalY=0 NormalZ=1 AngleXU=0 Radius=16 StartAngle=3.45983 EndAngle=5.96495
    g13: GeomPoint X=0 Y=-27.5 Z=0
    g14: LineSegment StartX=-50 StartY=0 StartZ=0 EndX=50 EndY=0 EndZ=0
    g15: LineSegment StartX=22.5 StartY=-7.1e-15 StartZ=0 EndX=27.5 EndY=-7.1e-15 EndZ=0
    g16: LineSegment StartX=15.1966 StartY=-8.26504 StartZ=0 EndX=-15.1966 EndY=-8.26504 EndZ=0
    g17: GeomPoint X=0 Y=-8.26504 Z=0
    g18: GeomPoint X=0 Y=0 Z=0
  constraints (51):
    c: Coincident(g1,g0)
    c: Vertical(g1)
    c: Coincident(g2,g1)
    c: Coincident(g3,g0)
    c: Vertical(g3)
    c: Coincident(g4,g3)
    c: Coincident(g5,g4)
    c: Vertical(g5)
    c: Coincident(g6,g5)
    c: Horizontal(g6)
    c: Vertical(g7)
    c: Coincident(g8,g7)
    c: Vertical(g9)
    c: Vertical(g10)
    c: Coincident(g12,g2)
    c: Coincident(g12,g11)
    c: Equal(g2,g11)
    c: Horizontal(g0)
    c: Equal(g3,g9)
    c: Equal(g8,g4)
    c: Symmetric(g7,g5,g13)
    c: PointOnObject(g13,g-2)
    c: Coincident(g6,g7)
    c: Coincident(g8,g9)
    c: Coincident(g10,g11)
    c: Equal(g1,g10)
    c: Equal(g5,g7)
    c: Parallel(g2,g4)
    c: Parallel(g11,g8)
    c: DistanceX(g0,g9) = 55
    c: PointOnObject(g0,g-1)
    c: Distance(g11) = 8
    c: DistanceX(g5,g6) = 38
    c: DistanceX(g0,g0) = 5
    c: DistanceY(g3,g3) = 16.7
    c: DistanceY(g1,g1) = 5
    c: Diameter(g12) = 32
    c: Horizontal(g14)
    c: DistanceX(g14,g14) = 100
    c: DistanceY(g5,g14) = 27.5
    c: DistanceY(g5,g5) = 7
    c: Coincident(g15,g10)
    c: Coincident(g15,g9)
    c: Horizontal(g15)
    c: Coincident(g16,g11)
    c: Coincident(g16,g2)
    c: Horizontal(g16)
    c: Symmetric(g11,g2,g17)
    c: PointOnObject(g17,g-2)
    c: Symmetric(g14,g14,g18)
    c: Coincident(g18,g-1)
FEATURE [PartDesign::Pad] Pad010
  BaseFeature = -> Pad009
  Direction = (1,1,1)
  Length = 10
  Length2 = 100
  Profile = -> Sketch022
  Type = 0
  expr: Length = Spreadsheet.lid_thicc
FEATURE [Sketcher::SketchObject] Sketch023
  ExternalGeometry = -> [Pad010]
  FullyConstrained = true
  MapMode = 5
  Placement = pos=(-10.803,-24.1646,0) rot=(0.95737,-0.204259,-0.204259;1.61435rad)
  Support = -> [Pad010]
  expr: Constraints[11] = Spreadsheet.tubing_dia / 2 + 2
  expr: Constraints[7] = Spreadsheet.tubing_dia / 2
  sketch-geometry (6):
    g0: LineSegment StartX=-15.6342 StartY=60.1 StartZ=0 EndX=-11.6342 EndY=60.1 EndZ=0
    g1: LineSegment StartX=-11.6342 StartY=60.1 StartZ=0 EndX=-11.6342 EndY=54.1 EndZ=0
    g2: LineSegment StartX=-15.6342 StartY=60.1 StartZ=0 EndX=-15.6342 EndY=54.1 EndZ=0
    g3: ArcOfCircle CenterX=-13.6342 CenterY=54.1 CenterZ=0 NormalX=0 NormalY=0 NormalZ=1 AngleXU=0 Radius=2 StartAngle=3.14159 EndAngle=6.28319
    g4: GeomPoint X=-13.6342 Y=60.1 Z=0
    g5: GeomPoint X=-13.6342 Y=50.1 Z=0
  constraints (12):
    c: Horizontal(g0)
    c: Coincident(g1,g0)
    c: Vertical(g1)
    c: Coincident(g2,g0)
    c: Vertical(g2)
    c: Tangent(g3,g1) = 1.5708
    c: Tangent(g3,g2) = -1.5708
    c: Radius(g3) = 2
    c: Symmetric(g0,g0,g4)
    c: Symmetric(g-3,g-3,g4)
    c: Symmetric(g-4,g-4,g5)
    c: DistanceY(g5,g3) = 4
FEATURE [PartDesign::Pocket] Pocket011
  BaseFeature = -> Pad010
  Length = 5
  Length2 = 100
  Profile = -> Sketch023
  Type = 1
FEATURE [PartDesign::Mirrored] Mirrored
  BaseFeature = -> Pocket011
  MirrorPlane = -> YZ_Plane016
  Originals = -> [Pocket011]
FEATURE [Sketcher::SketchObject] Sketch024
  AttachmentOffset = pos=(0,0,50.1) rot=(0,0,1;0rad)
  FullyConstrained = true
  MapMode = 5
  Placement = pos=(0,0,50.1) rot=(0,0,1;0rad)
  Support = -> [XY_Plane016]
  expr: Constraints[23] = Spreadsheet.lower_mount_holes_dist_to_origin_x
  expr: Constraints[25] = Spreadsheet.lower_mount_holes_dist_to_origin_y
  expr: Constraints[21] = Spreadsheet.upper_mount_holes_dist_to_origin
  expr: Constraints[17] = Spreadsheet.mount_holes_dia / 2
  expr: Constraints[22] = Spreadsheet.upper_mount_holes_dist_to_origin
  expr: Constraints[20] = Spreadsheet.upper_mount_holes_dist_to_origin
  expr: .AttachmentOffset.Base.z = Spreadsheet.casing_offset + Spreadsheet.base_thicc
  expr: Constraints[13] = Spreadsheet.base_construction_circle_dia / 2
  sketch-geometry (9):
    g0: Circle CenterX=0 CenterY=0 CenterZ=0 NormalX=0 NormalY=0 NormalZ=1 AngleXU=0 Radius=15
    g1: Circle CenterX=15.495 CenterY=15.495 CenterZ=0 NormalX=0 NormalY=0 NormalZ=1 AngleXU=0 Radius=1.5
    g2: Circle CenterX=15.495 CenterY=-15.495 CenterZ=0 NormalX=0 NormalY=0 NormalZ=1 AngleXU=0 Radius=1.5
    g3: Circle CenterX=-15.495 CenterY=-15.495 CenterZ=0 NormalX=0 NormalY=0 NormalZ=1 AngleXU=0 Radius=1.5
    g4: Circle CenterX=-15.495 CenterY=15.495 CenterZ=0 NormalX=0 NormalY=0 NormalZ=1 AngleXU=0 Radius=1.5
    g5: Circle CenterX=-19.5 CenterY=19.5 CenterZ=0 NormalX=0 NormalY=0 NormalZ=1 AngleXU=0 Radius=2
    g6: Circle CenterX=-13.5 CenterY=-19.5 CenterZ=0 NormalX=0 NormalY=0 NormalZ=1 AngleXU=0 Radius=2
    g7: Circle CenterX=13.5 CenterY=-19.5 CenterZ=0 NormalX=0 NormalY=0 NormalZ=1 AngleXU=0 Radius=2
    g8: Circle CenterX=19.5 CenterY=19.5 CenterZ=0 NormalX=0 NormalY=0 NormalZ=1 AngleXU=0 Radius=2
  constraints (26):
    c: Coincident(g0,g-1)
    c: DistanceX(g4,g1) = 30.99
    c: DistanceX(g3,g2) = 30.99
    c: DistanceY(g2,g1) = 30.99
    c: DistanceY(g3,g4) = 30.99
    c: DistanceY(g3,g0) = 15.495
    c: DistanceX(g3,g0) = 15.495
    c: DistanceY(g0,g1) = 15.495
    c: DistanceX(g0,g1) = 15.495
    c: Equal(g2,g3)
    c: Equal(g3,g4)
    c: Equal(g4,g1)
    c: Radius(g2) = 1.5
    c: Radius(g0) = 15
    c: Equal(g8,g5)
    c: Equal(g8,g7)
    c: Equal(g7,g6)
    c: Radius(g5) = 2
    c: Horizontal(g7,g6)
    c: Horizontal(g8,g5)
    c: DistanceX(g5,g0) = 19.5
    c: DistanceY(g0,g5) = 19.5
    c: DistanceX(g0,g8) = 19.5
    c: DistanceX(g6,g0) = 13.5
    c: DistanceX(g0,g7) = 13.5
    c: DistanceY(g7,g0) = 19.5
FEATURE [PartDesign::Pocket] Pocket012
  BaseFeature = -> Mirrored
  Length = 5
  Length2 = 100
  Midplane = true
  Profile = -> Sketch024
  Type = 1
FEATURE [Sketcher::SketchObject] Sketch025
  AttachmentOffset = pos=(0,0,70.1) rot=(0,0,1;0rad)
  FullyConstrained = true
  MapMode = 5
  Placement = pos=(0,0,70.1) rot=(0,0,1;0rad)
  Support = -> [XY_Plane017]
  expr: .AttachmentOffset.Base.z = Spreadsheet.casing_offset + Spreadsheet.base_thicc + 2 * Spreadsheet.lid_thicc
  expr: Constraints[16] = Spreadsheet.base_length
  expr: Constraints[15] = Spreadsheet.base_width
  sketch-geometry (10):
    g0: LineSegment StartX=-27.5 StartY=25.5 StartZ=0 EndX=-27.5 EndY=-25.5 EndZ=0
    g1: LineSegment StartX=-25.5 StartY=-27.5 StartZ=0 EndX=25.5 EndY=-27.5 EndZ=0
    g2: LineSegment StartX=27.5 StartY=-25.5 StartZ=0 EndX=27.5 EndY=25.5 EndZ=0
    g3: LineSegment StartX=25.5 StartY=27.5 StartZ=0 EndX=-25.5 EndY=27.5 EndZ=0
    g4: ArcOfCircle CenterX=25.5 CenterY=25.5 CenterZ=0 NormalX=0 NormalY=0 NormalZ=1 AngleXU=0 Radius=2 StartAngle=0 EndAngle=1.5708
    g5: ArcOfCircle CenterX=25.5 CenterY=-25.5 CenterZ=0 NormalX=0 NormalY=0 NormalZ=1 AngleXU=0 Radius=2 StartAngle=4.71239 EndAngle=6.28319
    g6: ArcOfCircle CenterX=-25.5 CenterY=-25.5 CenterZ=0 NormalX=0 NormalY=0 NormalZ=1 AngleXU=0 Radius=2 StartAngle=3.14159 EndAngle=4.71239
    g7: ArcOfCircle CenterX=-25.5 CenterY=25.5 CenterZ=0 NormalX=0 NormalY=0 NormalZ=1 AngleXU=0 Radius=2 StartAngle=1.5708 EndAngle=3.14159
    g8: GeomPoint X=0 Y=27.5 Z=0
    g9: GeomPoint X=27.5 Y=0 Z=0
  constraints (22):
    c: Vertical(g0)
    c: Horizontal(g1)
    c: Vertical(g2)
    c: Horizontal(g3)
    c: Tangent(g3,g4) = -1.5708
    c: Tangent(g2,g4) = -1.5708
    c: Tangent(g2,g5) = -1.5708
    c: Tangent(g1,g5) = -1.5708
    c: Tangent(g1,g6) = -1.5708
    c: Tangent(g0,g6) = -1.5708
    c: Tangent(g0,g7) = -1.5708
    c: Tangent(g3,g7) = -1.5708
    c: Equal(g1,g3)
    c: Equal(g0,g2)
    c: Equal(g7,g4)
    c: DistanceX(g0,g2) = 55
    c: DistanceY(g1,g3) = 55
    c: Symmetric(g3,g3,g8)
    c: Symmetric(g2,g2,g9)
    c: PointOnObject(g9,g-1)
    c: PointOnObject(g8,g-2)
    c: Radius(g4) = 2
FEATURE [Sketcher::SketchObject] Sketch026
  AttachmentOffset = pos=(0,0,40.1) rot=(0,0,1;0rad)
  FullyConstrained = true
  MapMode = 5
  Placement = pos=(0,0,40.1) rot=(0,0,1;0rad)
  Support = -> [XY_Plane016]
  expr: Constraints[79] = Spreadsheet.upper_mount_holes_dist_to_origin
  expr: .AttachmentOffset.Base.z = Spreadsheet.casing_offset
  expr: Constraints[78] = Spreadsheet.upper_mount_holes_dist_to_origin
  expr: Constraints[77] = Spreadsheet.lower_mount_holes_dist_to_origin_x
  expr: Constraints[76] = Spreadsheet.upper_mount_holes_dist_to_origin
  expr: Constraints[39] = Spreadsheet.upper_mount_holes_dist_to_origin
  expr: Constraints[38] = Spreadsheet.lower_mount_holes_dist_to_origin_x
  expr: Constraints[37] = Spreadsheet.lower_mount_holes_dist_to_origin_y
  expr: Constraints[36] = Spreadsheet.upper_mount_holes_dist_to_origin
  sketch-geometry (28):
    g0: LineSegment StartX=22.9641 StartY=17.5 StartZ=0 EndX=22.9641 EndY=21.5 EndZ=0
    g1: LineSegment StartX=22.9641 StartY=21.5 StartZ=0 EndX=19.5 EndY=23.5 EndZ=0
    g2: LineSegment StartX=19.5 StartY=23.5 StartZ=0 EndX=16.0359 EndY=21.5 EndZ=0
    g3: LineSegment StartX=16.0359 StartY=21.5 StartZ=0 EndX=16.0359 EndY=17.5 EndZ=0
    g4: LineSegment StartX=16.0359 StartY=17.5 StartZ=0 EndX=19.5 EndY=15.5 EndZ=0
    g5: LineSegment StartX=19.5 StartY=15.5 StartZ=0 EndX=22.9641 EndY=17.5 EndZ=0
    g6: Circle CenterX=19.5 CenterY=19.5 CenterZ=0 NormalX=0 NormalY=0 NormalZ=1 AngleXU=0 Radius=4
    g7: LineSegment StartX=16.9641 StartY=-21.5 StartZ=0 EndX=16.9641 EndY=-17.5 EndZ=0
    g8: LineSegment StartX=16.9641 StartY=-17.5 StartZ=0 EndX=13.5 EndY=-15.5 EndZ=0
    g9: LineSegment StartX=13.5 StartY=-15.5 StartZ=0 EndX=10.0359 EndY=-17.5 EndZ=0
    g10: LineSegment StartX=10.0359 StartY=-17.5 StartZ=0 EndX=10.0359 EndY=-21.5 EndZ=0
    g11: LineSegment StartX=10.0359 StartY=-21.5 StartZ=0 EndX=13.5 EndY=-23.5 EndZ=0
    g12: LineSegment StartX=13.5 StartY=-23.5 StartZ=0 EndX=16.9641 EndY=-21.5 EndZ=0
    g13: Circle CenterX=13.5 CenterY=-19.5 CenterZ=0 NormalX=0 NormalY=0 NormalZ=1 AngleXU=0 Radius=4
    g14: LineSegment StartX=-10.0359 StartY=-21.5 StartZ=0 EndX=-10.0359 EndY=-17.5 EndZ=0
    g15: LineSegment StartX=-10.0359 StartY=-17.5 StartZ=0 EndX=-13.5 EndY=-15.5 EndZ=0
    g16: LineSegment StartX=-13.5 StartY=-15.5 StartZ=0 EndX=-16.9641 EndY=-17.5 EndZ=0
    g17: LineSegment StartX=-16.9641 StartY=-17.5 StartZ=0 EndX=-16.9641 EndY=-21.5 EndZ=0
    g18: LineSegment StartX=-16.9641 StartY=-21.5 StartZ=0 EndX=-13.5 EndY=-23.5 EndZ=0
    g19: LineSegment StartX=-13.5 StartY=-23.5 StartZ=0 EndX=-10.0359 EndY=-21.5 EndZ=0
    g20: Circle CenterX=-13.5 CenterY=-19.5 CenterZ=0 NormalX=0 NormalY=0 NormalZ=1 AngleXU=0 Radius=4
    g21: LineSegment StartX=-16.0359 StartY=17.5 StartZ=0 EndX=-16.0359 EndY=21.5 EndZ=0
    g22: LineSegment StartX=-16.0359 StartY=21.5 StartZ=0 EndX=-19.5 EndY=23.5 EndZ=0
    g23: LineSegment StartX=-19.5 StartY=23.5 StartZ=0 EndX=-22.9641 EndY=21.5 EndZ=0
    g24: LineSegment StartX=-22.9641 StartY=21.5 StartZ=0 EndX=-22.9641 EndY=17.5 EndZ=0
    g25: LineSegment StartX=-22.9641 StartY=17.5 StartZ=0 EndX=-19.5 EndY=15.5 EndZ=0
    g26: LineSegment StartX=-19.5 StartY=15.5 StartZ=0 EndX=-16.0359 EndY=17.5 EndZ=0
    g27: Circle CenterX=-19.5 CenterY=19.5 CenterZ=0 NormalX=0 NormalY=0 NormalZ=1 AngleXU=0 Radius=4
  constraints (68):
    c: Coincident(g0,g1)
    c: Coincident(g1,g2)
    c: Coincident(g2,g3)
    c: Coincident(g3,g4)
    c: Coincident(g4,g5)
    c: Coincident(g5,g0)
    c: Equal(g0, g1-g5) x5
    c: PointOnObject(g0,g6)
    c: PointOnObject(g1,g6)
    c: PointOnObject(g2,g6)
    c: PointOnObject(g3,g6)
    c: PointOnObject(g4,g6)
    c: PointOnObject(g5,g6)
    c: Coincident(g7,g8)
    c: Coincident(g8,g9)
    c: Coincident(g9,g10)
    c: Coincident(g10,g11)
    c: Coincident(g11,g12)
    c: Coincident(g12,g7)
    c: Equal(g7, g8-g12) x5
    c: PointOnObject(g7,g13)
    c: PointOnObject(g8,g13)
    c: PointOnObject(g9,g13)
    c: PointOnObject(g10,g13)
    c: PointOnObject(g11,g13)
    c: PointOnObject(g12,g13)
    c: Radius(g13) = 4
    c: Radius(g6) = 4
    c: DistanceY(g-1,g6) = 19.5
    c: DistanceY(g13,g-1) = 19.5
    c: DistanceX(g-1,g13) = 13.5
    c: DistanceX(g-1,g6) = 19.5
    c: Coincident(g14,g15)
    c: Coincident(g15,g16)
    c: Coincident(g16,g17)
    c: Coincident(g17,g18)
    c: Coincident(g18,g19)
    c: Coincident(g19,g14)
    c: Equal(g14, g15-g19) x5
    c: PointOnObject(g14,g20)
    c: PointOnObject(g15,g20)
    c: PointOnObject(g16,g20)
    c: PointOnObject(g17,g20)
    c: PointOnObject(g18,g20)
    c: PointOnObject(g19,g20)
    c: Coincident(g21,g22)
    c: Coincident(g22,g23)
    c: Coincident(g23,g24)
    c: Coincident(g24,g25)
    c: Coincident(g25,g26)
    c: Coincident(g26,g21)
    c: Equal(g21, g22-g26) x5
    c: PointOnObject(g21,g27)
    c: PointOnObject(g22,g27)
    c: PointOnObject(g23,g27)
    c: PointOnObject(g24,g27)
    c: PointOnObject(g25,g27)
    c: PointOnObject(g26,g27)
    c: Radius(g27) = 4
    c: Radius(g20) = 4
    c: DistanceY(g20,g-1) = 19.5
    c: DistanceX(g20,g-1) = 13.5
    c: DistanceX(g27,g-1) = 19.5
    c: DistanceY(g-1,g27) = 19.5
    c: Vertical(g10)
    c: Vertical(g14)
    c: Vertical(g3)
    c: Vertical(g21)
FEATURE [PartDesign::Pocket] Pocket013
  BaseFeature = -> Pocket012
  Length = 3
  Length2 = 100
  Profile = -> Sketch026
  Reversed = true
  Type = 0
FEATURE [PartDesign::Body] Body007  label="base"
  Group = -> [Sketch021,Pad009,Sketch022,Pad010,Sketch023,Pocket011,Mirrored,Sketch024,Pocket012,Sketch026,Pocket013]
  Origin = -> Origin016
  Tip = -> Pocket013
FEATURE [PartDesign::Pad] Pad011
  Direction = (1,1,1)
  Length = 10
  Length2 = 100
  Profile = -> Sketch025
  Reversed = true
  Type = 0
  expr: Length = Spreadsheet.lid_thicc
FEATURE [Sketcher::SketchObject] Sketch027
  AttachmentOffset = pos=(0,0,60.1) rot=(0,0,1;0rad)
  FullyConstrained = true
  MapMode = 5
  Placement = pos=(0,0,60.1) rot=(0,0,1;0rad)
  Support = -> [XY_Plane017]
  expr: .AttachmentOffset.Base.z = Spreadsheet.casing_offset + Spreadsheet.base_thicc + Spreadsheet.lid_thicc
  expr: Constraints[6] = Spreadsheet.tubing_dia - 0.1
  sketch-geometry (4):
    g0: LineSegment StartX=-19.9456 StartY=-6.25 StartZ=0 EndX=-16.38 EndY=-7.83 EndZ=0
    g1: LineSegment StartX=-21.4441 StartY=-19.2582 StartZ=0 EndX=-16.38 EndY=-7.83 EndZ=0
    g2: LineSegment StartX=-19.9456 StartY=-6.25 StartZ=0 EndX=-25.0097 EndY=-17.6782 EndZ=0
    g3: LineSegment StartX=-25.0097 StartY=-17.6782 StartZ=0 EndX=-21.4441 EndY=-19.2582 EndZ=0
  constraints (12):
    c: Coincident(g1,g0)
    c: Coincident(g2,g0)
    c: Coincident(g3,g2)
    c: Coincident(g3,g1)
    c: Equal(g1,g2)
    c: Equal(g0,g3)
    c: Distance(g3) = 3.9
    c: Perpendicular(g3,g2)
    c: Distance(g1) = 12.5
    c: DistanceX(g0,g-1) = 16.38
    c: DistanceY(g0,g-1) = 6.25
    c: DistanceY(g0,g-1) = 7.83
FEATURE [PartDesign::Pad] Pad012
  BaseFeature = -> Pad011
  Direction = (1,1,1)
  Length = 6
  Length2 = 100
  Profile = -> Sketch027
  Reversed = true
  Type = 0
  expr: Length = Spreadsheet.lid_thicc - Spreadsheet.tubing_dia
FEATURE [Sketcher::SketchObject] Sketch028
  ExternalGeometry = -> [Pad012]
  FullyConstrained = true
  MapMode = 5
  Placement = pos=(-10.6527,-24.0401,0) rot=(0.958011,-0.20275,-0.20275;1.61368rad)
  Support = -> [Pad012]
  sketch-geometry (3):
    g0: GeomPoint X=-13.7534 Y=54.1 Z=0
    g1: ArcOfCircle CenterX=-13.7534 CenterY=54.1 CenterZ=0 NormalX=0 NormalY=0 NormalZ=1 AngleXU=0 Radius=1.95 StartAngle=4.2e-15 EndAngle=3.14159
    g2: LineSegment StartX=-11.8034 StartY=54.1 StartZ=0 EndX=-15.7034 EndY=54.1 EndZ=0
  constraints (6):
    c: Symmetric(g-3,g-3,g0)
    c: Coincident(g1,g0)
    c: Coincident(g1,g-3)
    c: Coincident(g1,g-3)
    c: Coincident(g2,g1)
    c: Coincident(g2,g1)
FEATURE [PartDesign::Pocket] Pocket014
  BaseFeature = -> Pad012
  Length = 5
  Length2 = 100
  Profile = -> Sketch028
  Type = 1
FEATURE [PartDesign::Mirrored] Mirrored001
  BaseFeature = -> Pocket014
  MirrorPlane = -> YZ_Plane017
  Originals = -> [Pad012,Pocket014]
FEATURE [Sketcher::SketchObject] Sketch029
  AttachmentOffset = pos=(0,0,60.1) rot=(0,0,1;0rad)
  FullyConstrained = true
  MapMode = 5
  Placement = pos=(0,0,60.1) rot=(0,0,1;0rad)
  Support = -> [XY_Plane017]
  expr: Constraints[19] = Spreadsheet.lower_mount_holes_dist_to_origin_x
  expr: Constraints[18] = Spreadsheet.lower_mount_holes_dist_to_origin_y
  expr: Constraints[16] = Spreadsheet.upper_mount_holes_dist_to_origin
  expr: Constraints[20] = Spreadsheet.lower_mount_holes_dist_to_origin_x
  expr: Constraints[15] = Spreadsheet.upper_mount_holes_dist_to_origin
  expr: Constraints[17] = Spreadsheet.lower_mount_holes_dist_to_origin_y
  expr: Constraints[14] = Spreadsheet.upper_mount_holes_dist_to_origin
  expr: Constraints[13] = Spreadsheet.upper_mount_holes_dist_to_origin
  expr: Constraints[7] = Spreadsheet.base_construction_circle_dia / 2
  expr: .AttachmentOffset.Base.z = Spreadsheet.casing_offset + 2 * Spreadsheet.base_thicc
  expr: Constraints[3] = Spreadsheet.mount_holes_dia / 2
  sketch-geometry (8):
    g0: Circle CenterX=19.5 CenterY=19.5 CenterZ=0 NormalX=0 NormalY=0 NormalZ=1 AngleXU=0 Radius=2
    g1: Circle CenterX=-19.5 CenterY=19.5 CenterZ=0 NormalX=0 NormalY=0 NormalZ=1 AngleXU=0 Radius=2
    g2: Circle CenterX=-13.5 CenterY=-19.5 CenterZ=0 NormalX=0 NormalY=0 NormalZ=1 AngleXU=0 Radius=2
    g3: Circle CenterX=13.5 CenterY=-19.5 CenterZ=0 NormalX=0 NormalY=0 NormalZ=1 AngleXU=0 Radius=2
    g4: ArcOfCircle CenterX=0 CenterY=0 CenterZ=0 NormalX=0 NormalY=0 NormalZ=1 AngleXU=0 Radius=15 StartAngle=3.71572 EndAngle=5.70906
    g5: LineSegment StartX=-12.595 StartY=-8.14653 StartZ=0 EndX=12.595 EndY=-8.14653 EndZ=0
    g6: GeomPoint X=1.7e-15 Y=-8.14653 Z=0
    g7: Circle CenterX=0 CenterY=0 CenterZ=0 NormalX=0 NormalY=0 NormalZ=1 AngleXU=0 Radius=4.6
  constraints (21):
    c: Equal(g0,g1)
    c: Equal(g0,g3)
    c: Equal(g3,g2)
    c: Radius(g1) = 2
    c: Coincident(g5,g4)
    c: Coincident(g5,g4)
    c: Horizontal(g5)
    c: Radius(g4) = 15
    c: DistanceX(g5,g5) = 25.19
    c: Symmetric(g4,g4,g6)
    c: Coincident(g4,g-1)
    c: Coincident(g7,g4)
    c: Radius(g7) = 4.6
    c: DistanceX(g1,g4) = 19.5
    c: DistanceY(g4,g0) = 19.5
    c: DistanceX(g4,g0) = 19.5
    c: DistanceY(g4,g1) = 19.5
    c: DistanceY(g3,g4) = 19.5
    c: DistanceY(g2,g4) = 19.5
    c: DistanceX(g4,g3) = 13.5
    c: DistanceX(g2,g4) = 13.5
FEATURE [PartDesign::Pocket] Pocket015
  BaseFeature = -> Mirrored001
  Length = 5
  Length2 = 100
  Profile = -> Sketch029
  Reversed = true
  Type = 1
FEATURE [Sketcher::SketchObject] Sketch030
  AttachmentOffset = pos=(0,0,70.1) rot=(0,0,1;0rad)
  FullyConstrained = true
  MapMode = 5
  Placement = pos=(0,0,70.1) rot=(0,0,1;0rad)
  Support = -> [XY_Plane017]
  expr: Constraints[11] = Spreadsheet.lower_mount_holes_dist_to_origin_x
  expr: Constraints[9] = Spreadsheet.lower_mount_holes_dist_to_origin_y
  expr: Constraints[8] = Spreadsheet.lower_mount_holes_dist_to_origin_y
  expr: .AttachmentOffset.Base.z = Spreadsheet.base_thicc + Spreadsheet.casing_offset + Spreadsheet.lid_thicc * 2
  expr: Constraints[7] = Spreadsheet.upper_mount_holes_dist_to_origin
  expr: Constraints[6] = Spreadsheet.upper_mount_holes_dist_to_origin
  expr: Constraints[10] = Spreadsheet.lower_mount_holes_dist_to_origin_x
  expr: Constraints[5] = Spreadsheet.upper_mount_holes_dist_to_origin
  expr: Constraints[4] = Spreadsheet.upper_mount_holes_dist_to_origin
  sketch-geometry (4):
    g0: Circle CenterX=13.5 CenterY=-19.5 CenterZ=0 NormalX=0 NormalY=0 NormalZ=1 AngleXU=0 Radius=4
    g1: Circle CenterX=-13.5 CenterY=-19.5 CenterZ=0 NormalX=0 NormalY=0 NormalZ=1 AngleXU=0 Radius=4
    g2: Circle CenterX=-19.5 CenterY=19.5 CenterZ=0 NormalX=0 NormalY=0 NormalZ=1 AngleXU=0 Radius=4
    g3: Circle CenterX=19.5 CenterY=19.5 CenterZ=0 NormalX=0 NormalY=0 NormalZ=1 AngleXU=0 Radius=4
  constraints (12):
    c: Equal(g2,g3)
    c: Equal(g3,g0)
    c: Equal(g0,g1)
    c: Radius(g2) = 4
    c: DistanceX(g2,g-1) = 19.5
    c: DistanceX(g-1,g3) = 19.5
    c: DistanceY(g-1,g3) = 19.5
    c: DistanceY(g-1,g2) = 19.5
    c: DistanceY(g0,g-1) = 19.5
    c: DistanceY(g1,g-1) = 19.5
    c: DistanceX(g-1,g0) = 13.5
    c: DistanceX(g1,g-1) = 13.5
FEATURE [PartDesign::Pocket] Pocket016
  BaseFeature = -> Pocket015
  Length = 3
  Length2 = 100
  Profile = -> Sketch030
  Type = 0
FEATURE [Sketcher::SketchObject] Sketch031
  AttachmentOffset = pos=(0,0,60.1) rot=(0,0,1;0rad)
  FullyConstrained = true
  MapMode = 5
  Placement = pos=(0,0,60.1) rot=(0,0,1;0rad)
  Support = -> [XY_Plane017]
  expr: .AttachmentOffset.Base.z = Spreadsheet.casing_offset + Spreadsheet.base_thicc + Spreadsheet.lid_thicc
  expr: Constraints[1] = Spreadsheet.base_construction_circle_dia / 2
  sketch-geometry (1):
    g0: Circle CenterX=0 CenterY=0 CenterZ=0 NormalX=0 NormalY=0 NormalZ=1 AngleXU=0 Radius=15
  constraints (2):
    c: Coincident(g0,g-1)
    c: Radius(g0) = 15
FEATURE [PartDesign::Pocket] Pocket017
  BaseFeature = -> Pocket016
  Length = 8.5
  Length2 = 100
  Profile = -> Sketch031
  Reversed = true
  Type = 0
  expr: Length = Spreadsheet.lid_thicc - 1.5
FEATURE [PartDesign::Body] Body008  label="top"
  Group = -> [Sketch025,Pad011,Sketch027,Pad012,Sketch028,Pocket014,Mirrored001,Sketch029,Pocket015,Sketch030,Pocket016,Sketch031,Pocket017]
  Origin = -> Origin017
  Tip = -> Pocket017
FEATURE [Sketcher::SketchObject] Sketch032
  AttachmentOffset = pos=(0,0,50.1) rot=(0,0,1;0rad)
  FullyConstrained = true
  MapMode = 5
  Placement = pos=(0,0,50.1) rot=(0,0,1;0rad)
  Support = -> [XY_Plane018]
  expr: Constraints[38] = Spreadsheet.base_construction_circle_dia + Spreadsheet.tubing_dia + 1.74
  expr: Constraints[14] = Spreadsheet.base_length / 2 - 0.5
  expr: .AttachmentOffset.Base.z = Spreadsheet.casing_offset + Spreadsheet.base_thicc
  expr: Constraints[13] = Spreadsheet.base_width
  expr: Constraints[5] = Spreadsheet.base_length / 2
  sketch-geometry (15):
    g0: LineSegment StartX=-25.5 StartY=27.5 StartZ=0 EndX=25.5 EndY=27.5 EndZ=0
    g1: LineSegment StartX=-27.5 StartY=25.5 StartZ=0 EndX=-27.5 EndY=0.5 EndZ=0
    g2: LineSegment StartX=27.5 StartY=25.5 StartZ=0 EndX=27.5 EndY=0.5 EndZ=0
    g3: GeomPoint X=0 Y=27.5 Z=0
    g4: ArcOfCircle CenterX=-25.5 CenterY=25.5 CenterZ=0 NormalX=0 NormalY=0 NormalZ=1 AngleXU=0 Radius=2 StartAngle=1.5708 EndAngle=3.14159
    g5: ArcOfCircle CenterX=25.5 CenterY=25.5 CenterZ=0 NormalX=0 NormalY=0 NormalZ=1 AngleXU=0 Radius=2 StartAngle=0 EndAngle=1.5708
    g6: LineSegment StartX=27.5 StartY=0.5 StartZ=0 EndX=22.5 EndY=0.5 EndZ=0
    g7: LineSegment StartX=-27.5 StartY=0.5 StartZ=0 EndX=-22.5 EndY=0.5 EndZ=0
    g8: LineSegment StartX=-22.5 StartY=0.5 StartZ=0 EndX=-22.5 EndY=-4.5 EndZ=0
    g9: LineSegment StartX=22.5 StartY=0.5 StartZ=0 EndX=22.5 EndY=-4.5 EndZ=0
    g10: LineSegment StartX=22.5 StartY=-4.5 StartZ=0 EndX=21.634 EndY=-5 EndZ=0
    g11: LineSegment StartX=21.634 StartY=-5 StartZ=0 EndX=17.4025 EndY=4.06062 EndZ=0
    g12: LineSegment StartX=-22.5 StartY=-4.5 StartZ=0 EndX=-21.634 EndY=-5 EndZ=0
    g13: LineSegment StartX=-21.634 StartY=-5 StartZ=0 EndX=-17.4025 EndY=4.06062 EndZ=0
    g14: ArcOfCircle CenterX=0 CenterY=0 CenterZ=0 NormalX=0 NormalY=0 NormalZ=1 AngleXU=0 Radius=17.87 StartAngle=0.229234 EndAngle=2.91236
  constraints (41):
    c: Horizontal(g0)
    c: Vertical(g1)
    c: Vertical(g2)
    c: PointOnObject(g3,g-2)
    c: Equal(g1,g2)
    c: DistanceY(g-1,g3) = 27.5
    c: Tangent(g0,g4) = 1.5708
    c: Tangent(g1,g4) = -1.5708
    c: Tangent(g0,g5) = 1.5708
    c: Tangent(g2,g5) = 1.5708
    c: Radius(g5) = 2
    c: Symmetric(g0,g0,g3)
    c: Radius(g4) = 2
    c: DistanceX(g1,g2) = 55
    c: DistanceY(g1,g0) = 27
    c: Coincident(g6,g2)
    c: Horizontal(g6)
    c: Coincident(g7,g1)
    c: Horizontal(g7)
    c: Coincident(g8,g7)
    c: Vertical(g8)
    c: Coincident(g9,g6)
    c: Vertical(g9)
    c: Equal(g6,g7)
    c: Equal(g9,g8)
    c: DistanceX(g6,g6) = 5
    c: DistanceY(g9,g9) = 5
    c: Coincident(g10,g9)
    c: Coincident(g11,g10)
    c: Coincident(g12,g8)
    c: Coincident(g13,g12)
    c: Equal(g11,g13)
    c: Equal(g12,g10)
    c: Distance(g10) = 1
    c: Distance(g13) = 10
    c: Coincident(g14,g-1)
    c: Coincident(g14,g13)
    c: Coincident(g14,g11)
    c: Diameter(g14) = 35.74
    c: Angle(g12,g8) = 2.0944
    c: Angle(g9,g10) = 2.0944
FEATURE [PartDesign::Pad] Pad013
  Direction = (1,1,1)
  Length = 10
  Length2 = 100
  Profile = -> Sketch032
  Type = 0
  expr: Length = Spreadsheet.lid_thicc
FEATURE [Sketcher::SketchObject] Sketch033
  AttachmentOffset = pos=(0,0,50.1) rot=(0,0,1;0rad)
  FullyConstrained = true
  MapMode = 5
  Placement = pos=(0,0,50.1) rot=(0,0,1;0rad)
  Support = -> [XY_Plane018]
  expr: .AttachmentOffset.Base.z = Spreadsheet.casing_offset + Spreadsheet.base_thicc
  expr: Constraints[4] = Spreadsheet.upper_mount_holes_dist_to_origin
  expr: Constraints[3] = Spreadsheet.upper_mount_holes_dist_to_origin
  expr: Constraints[5] = Spreadsheet.upper_mount_holes_dist_to_origin
  expr: Constraints[2] = Spreadsheet.upper_mount_holes_dist_to_origin
  expr: Constraints[1] = Spreadsheet.mount_holes_dia
  sketch-geometry (2):
    g0: Circle CenterX=19.5 CenterY=19.5 CenterZ=0 NormalX=0 NormalY=0 NormalZ=1 AngleXU=0 Radius=2
    g1: Circle CenterX=-19.5 CenterY=19.5 CenterZ=0 NormalX=0 NormalY=0 NormalZ=1 AngleXU=0 Radius=2
  constraints (6):
    c: Equal(g0,g1)
    c: Diameter(g1) = 4
    c: DistanceX(g1,g-1) = 19.5
    c: DistanceY(g-1,g1) = 19.5
    c: DistanceY(g-1,g0) = 19.5
    c: DistanceX(g-1,g0) = 19.5
FEATURE [PartDesign::Pocket] Pocket018
  BaseFeature = -> Pad013
  Length = 5
  Length2 = 100
  Profile = -> Sketch033
  Reversed = true
  Type = 1
FEATURE [PartDesign::Body] Body009  label="tube-support"
  Group = -> [Sketch032,Pad013,Sketch033,Pocket018]
  Origin = -> Origin018
  Tip = -> Pocket018
FEATURE [Sketcher::SketchObject] Sketch034
  AttachmentOffset = pos=(0,0,40.1) rot=(0,0,1;0rad)
  FullyConstrained = true
  MapMode = 5
  Placement = pos=(0,0,40.1) rot=(0,0,1;0rad)
  Support = -> [XY_Plane019]
  expr: .AttachmentOffset.Base.z = Spreadsheet.casing_offset
  expr: Constraints[1] = Spreadsheet.bearing_hub_dia
  sketch-geometry (1):
    g0: Circle CenterX=0 CenterY=0 CenterZ=0 NormalX=0 NormalY=0 NormalZ=1 AngleXU=0 Radius=14.5
  constraints (2):
    c: Coincident(g0,g-1)
    c: Diameter(g0) = 29
FEATURE [PartDesign::Pad] Pad014
  Direction = (1,1,1)
  Length = 5
  Length2 = 100
  Profile = -> Sketch034
  Type = 0
  expr: Length = Spreadsheet.bearing_hub_thicc
FEATURE [Sketcher::SketchObject] Sketch035
  AttachmentOffset = pos=(0,0,45.1) rot=(0,0,1;0rad)
  FullyConstrained = true
  MapMode = 5
  Placement = pos=(0,0,45.1) rot=(0,0,1;0rad)
  Support = -> [XY_Plane019]
  expr: Constraints[1] = Spreadsheet.bearing_stp_motor_bevel_dia
  expr: .AttachmentOffset.Base.z = Spreadsheet.casing_offset + Spreadsheet.bearing_hub_thicc
  sketch-geometry (1):
    g0: Circle CenterX=0 CenterY=0 CenterZ=0 NormalX=0 NormalY=0 NormalZ=1 AngleXU=0 Radius=4.25
  constraints (2):
    c: Coincident(g0,g-1)
    c: Diameter(g0) = 8.5
FEATURE [PartDesign::Pad] Pad015
  BaseFeature = -> Pad014
  Direction = (1,1,1)
  Length = 1.5
  Length2 = 100
  Profile = -> Sketch035
  Type = 0
  expr: Length = Spreadsheet.bearing_stp_motor_bevel_height
FEATURE [Sketcher::SketchObject] Sketch036
  AttachmentOffset = pos=(0,0,45.1) rot=(0,0,1;0rad)
  FullyConstrained = true
  MapMode = 5
  Placement = pos=(0,0,45.1) rot=(0,0,1;0rad)
  Support = -> [XY_Plane019]
  expr: .AttachmentOffset.Base.z = Spreadsheet.casing_offset + Spreadsheet.bearing_hub_thicc
  expr: Constraints[1] = Spreadsheet.mount_holes_dia
  expr: Constraints[0] = Spreadsheet.bearing_roller_dist_to_center
  sketch-geometry (1):
    g0: Circle CenterX=-10.0993 CenterY=-1.43 CenterZ=0 NormalX=0 NormalY=0 NormalZ=1 AngleXU=0 Radius=2
  constraints (3):
    c: Distance(g-1,g0) = 10.2
    c: Diameter(g0) = 4
    c: DistanceY(g0,g-1) = 1.43
FEATURE [PartDesign::Pocket] Pocket019
  BaseFeature = -> Pad015
  Length = 5
  Length2 = 100
  Profile = -> Sketch036
  Type = 1
FEATURE [Sketcher::SketchObject] Sketch037
  AttachmentOffset = pos=(0,0,45.1) rot=(0,0,1;0rad)
  FullyConstrained = true
  MapMode = 5
  Placement = pos=(0,0,45.1) rot=(0,0,1;0rad)
  Support = -> [XY_Plane019]
  expr: .AttachmentOffset.Base.z = Spreadsheet.casing_offset + Spreadsheet.bearing_hub_thicc
  expr: Constraints[9] = Spreadsheet.bearing_roller_dist_to_center
  expr: Constraints[2] = Spreadsheet.bearing_hub_dia
  sketch-geometry (4):
    g0: ArcOfCircle CenterX=-10.0993 CenterY=-1.43 CenterZ=0 NormalX=0 NormalY=0 NormalZ=1 AngleXU=0 Radius=4.25 StartAngle=4.81971 EndAngle=8.02798
    g1: LineSegment StartX=-10.835 StartY=2.75582 StartZ=0 EndX=-14.3413 EndY=2.1395 EndZ=0
    g2: LineSegment StartX=-9.64404 StartY=-5.65555 StartZ=0 EndX=-13.1836 EndY=-6.03687 EndZ=0
    g3: ArcOfCircle CenterX=0 CenterY=0 CenterZ=0 NormalX=0 NormalY=0 NormalZ=1 AngleXU=0 Radius=14.5 StartAngle=2.9935 EndAngle=3.571
  constraints (11):
    c: Coincident(g3,g-1)
    c: Coincident(g3,g1)
    c: Diameter(g3) = 29
    c: Diameter(g0) = 8.5
    c: Tangent(g1,g0) = -1.5708
    c: Tangent(g2,g0) = 1.5708
    c: Equal(g2,g1)
    c: Distance(g1) = 3.56
    c: Coincident(g2,g3)
    c: Distance(g0,g3) = 10.2
    c: DistanceY(g0,g3) = 1.43
FEATURE [PartDesign::Pocket] Pocket020
  BaseFeature = -> Pocket019
  Length = 2.5
  Length2 = 100
  Profile = -> Sketch037
  Type = 0
  expr: Length = Spreadsheet.bearing_hub_pad_depth
FEATURE [PartDesign::PolarPattern] PolarPattern
  Angle = 360
  Axis = -> Sketch036 [N_Axis]
  BaseFeature = -> Pocket020
  Occurrences = 3
  Originals = -> [Pocket019,Pocket020]
FEATURE [Sketcher::SketchObject] Sketch038
  AttachmentOffset = pos=(0,0,45.1) rot=(0,0,1;0rad)
  FullyConstrained = true
  MapMode = 5
  Placement = pos=(0,0,45.1) rot=(0,0,1;0rad)
  Support = -> [XY_Plane019]
  expr: Constraints[4] = Spreadsheet.bearing_stp_motor_spindle_len
  expr: Constraints[5] = Spreadsheet.bearing_stp_motor_spindle_dia
  expr: .AttachmentOffset.Base.z = Spreadsheet.casing_offset + Spreadsheet.bearing_hub_thicc
  sketch-geometry (2):
    g0: LineSegment StartX=2 StartY=1.5 StartZ=0 EndX=2 EndY=-1.5 EndZ=0
    g1: ArcOfCircle CenterX=0 CenterY=0 CenterZ=0 NormalX=0 NormalY=0 NormalZ=1 AngleXU=0 Radius=2.5 StartAngle=0.643501 EndAngle=5.63968
  constraints (6):
    c: Vertical(g0)
    c: Coincident(g1,g-1)
    c: Coincident(g1,g0)
    c: Coincident(g1,g0)
    c: DistanceY(g0,g0) = 3
    c: Diameter(g1) = 5
FEATURE [PartDesign::Pocket] Pocket021
  BaseFeature = -> PolarPattern
  Length = 5
  Length2 = 100
  Midplane = true
  Profile = -> Sketch038
  Type = 1
FEATURE [PartDesign::Body] Body010  label="bearing-hub"
  Group = -> [Sketch034,Pad014,Sketch035,Pad015,Sketch036,Pocket019,Sketch037,Pocket020,PolarPattern,Sketch038,Pocket021]
  Origin = -> Origin019
  Tip = -> Pocket021
FEATURE [Sketcher::SketchObject] Sketch039
  AttachmentOffset = pos=(0,0,55.1) rot=(0,0,1;0rad)
  FullyConstrained = true
  MapMode = 5
  Placement = pos=(0,0,55.1) rot=(0,0,1;0rad)
  Support = -> [XY_Plane020]
  expr: .AttachmentOffset.Base.z = Spreadsheet.casing_offset + Spreadsheet.base_thicc + Spreadsheet.bearing_hub_thicc
  expr: Constraints[1] = Spreadsheet.bearing_hub_dia
  sketch-geometry (1):
    g0: Circle CenterX=0 CenterY=0 CenterZ=0 NormalX=0 NormalY=0 NormalZ=1 AngleXU=0 Radius=14.5
  constraints (2):
    c: Coincident(g0,g-1)
    c: Diameter(g0) = 29
FEATURE [PartDesign::Pad] Pad016
  Direction = (1,1,1)
  Length = 5
  Length2 = 100
  Profile = -> Sketch039
  Type = 0
  expr: Length = Spreadsheet.bearing_hub_thicc
FEATURE [Sketcher::SketchObject] Sketch040
  AttachmentOffset = pos=(0,0,60.1) rot=(0,0,1;0rad)
  FullyConstrained = true
  MapMode = 5
  Placement = pos=(0,0,60.1) rot=(0,0,1;0rad)
  Support = -> [XY_Plane020]
  expr: .AttachmentOffset.Base.z = Spreadsheet.casing_offset + Spreadsheet.base_thicc + Spreadsheet.bearing_hub_thicc * 2
  expr: Constraints[5] = Spreadsheet.bearing_hub_dia
  sketch-geometry (6):
    g0: LineSegment StartX=-14.4052 StartY=1.6551 StartZ=0 EndX=-8.51489 EndY=2.42155 EndZ=0
    g1: LineSegment StartX=-8.51489 StartY=2.42155 StartZ=0 EndX=-6.14817 EndY=-0.8 EndZ=0
    g2: LineSegment StartX=-6.14817 StartY=-0.8 StartZ=0 EndX=-7.61166 EndY=-4.51993 EndZ=0
    g3: LineSegment StartX=-7.61166 StartY=-4.51993 StartZ=0 EndX=-13.502 EndY=-5.28639 EndZ=0
    g4: ArcOfCircle CenterX=0 CenterY=0 CenterZ=0 NormalX=0 NormalY=0 NormalZ=1 AngleXU=0 Radius=14.5 StartAngle=3.0272 EndAngle=3.51477
    g5: LineSegment StartX=-8.51489 StartY=2.42155 StartZ=0 EndX=-7.61166 EndY=-4.51993 EndZ=0
  constraints (17):
    c: Coincident(g1,g0)
    c: Coincident(g2,g1)
    c: Coincident(g3,g2)
    c: Coincident(g4,g-1)
    c: Coincident(g4,g0)
    c: Diameter(g4) = 29
    c: Coincident(g3,g4)
    c: Equal(g3,g0)
    c: Parallel(g0,g3)
    c: Equal(g1,g2)
    c: Coincident(g5,g0)
    c: Coincident(g5,g2)
    c: Distance(g5) = 7
    c: Perpendicular(g0,g5)
    c: Distance(g1,g4) = 6.2
    c: Distance(g3) = 5.94
    c: DistanceY(g1,g4) = 0.8
FEATURE [PartDesign::Pocket] Pocket022
  BaseFeature = -> Pad016
  Length = 2.5
  Length2 = 100
  Profile = -> Sketch040
  Type = 0
  expr: Length = Spreadsheet.bearing_hub_pad_depth
FEATURE [Sketcher::SketchObject] Sketch041
  AttachmentOffset = pos=(0,0,55.1) rot=(0,0,1;0rad)
  FullyConstrained = true
  MapMode = 5
  Placement = pos=(0,0,55.1) rot=(0,0,1;0rad)
  Support = -> [XY_Plane020]
  expr: .AttachmentOffset.Base.z = Spreadsheet.casing_offset + Spreadsheet.base_thicc + Spreadsheet.bearing_hub_thicc
  expr: Constraints[1] = Spreadsheet.bearing_roller_dist_to_center
  expr: Constraints[0] = Spreadsheet.mount_holes_dia
  sketch-geometry (1):
    g0: Circle CenterX=-10.0993 CenterY=-1.43 CenterZ=0 NormalX=0 NormalY=0 NormalZ=1 AngleXU=0 Radius=2
  constraints (3):
    c: Diameter(g0) = 4
    c: Distance(g-1,g0) = 10.2
    c: DistanceY(g0,g-1) = 1.43
FEATURE [PartDesign::Pocket] Pocket023
  BaseFeature = -> Pocket022
  Length = 5
  Length2 = 100
  Profile = -> Sketch041
  Reversed = true
  Type = 1
FEATURE [PartDesign::PolarPattern] PolarPattern001
  Angle = 360
  Axis = -> Sketch041 [N_Axis]
  BaseFeature = -> Pocket023
  Occurrences = 3
  Originals = -> [Pocket023,Pocket022]
FEATURE [Sketcher::SketchObject] Sketch042
  AttachmentOffset = pos=(0,0,60.1) rot=(0,0,1;0rad)
  FullyConstrained = true
  MapMode = 5
  Placement = pos=(0,0,60.1) rot=(0,0,1;0rad)
  Support = -> [XY_Plane020]
  expr: .AttachmentOffset.Base.z = Spreadsheet.casing_offset + Spreadsheet.base_thicc + Spreadsheet.bearing_hub_thicc * 2
  expr: Constraints[1] = Spreadsheet.bearing_stp_motor_bevel_dia
  sketch-geometry (1):
    g0: Circle CenterX=0 CenterY=0 CenterZ=0 NormalX=0 NormalY=0 NormalZ=1 AngleXU=0 Radius=4.25
  constraints (2):
    c: Coincident(g0,g-1)
    c: Diameter(g0) = 8.5
FEATURE [PartDesign::Pad] Pad017
  BaseFeature = -> PolarPattern001
  Direction = (1,1,1)
  Length = 1.5
  Length2 = 100
  Profile = -> Sketch042
  Type = 0
  expr: Length = Spreadsheet.bearing_stp_motor_bevel_height
FEATURE [Sketcher::SketchObject] Sketch043
  AttachmentOffset = pos=(0,0,60.1) rot=(0,0,1;0rad)
  FullyConstrained = true
  MapMode = 5
  Placement = pos=(0,0,60.1) rot=(0,0,1;0rad)
  Support = -> [XY_Plane020]
  expr: .AttachmentOffset.Base.z = Spreadsheet.casing_offset + Spreadsheet.base_thicc + Spreadsheet.bearing_hub_thicc * 2
  expr: Constraints[5] = Spreadsheet.bearing_stp_motor_spindle_len
  expr: Constraints[4] = Spreadsheet.bearing_stp_motor_spindle_dia
  sketch-geometry (2):
    g0: LineSegment StartX=2 StartY=1.5 StartZ=0 EndX=2 EndY=-1.5 EndZ=0
    g1: ArcOfCircle CenterX=0 CenterY=0 CenterZ=0 NormalX=0 NormalY=0 NormalZ=1 AngleXU=0 Radius=2.5 StartAngle=0.643501 EndAngle=5.63968
  constraints (6):
    c: Vertical(g0)
    c: Coincident(g1,g-1)
    c: Coincident(g1,g0)
    c: Coincident(g1,g0)
    c: Diameter(g1) = 5
    c: DistanceY(g0,g0) = 3
FEATURE [PartDesign::Pocket] Pocket024
  BaseFeature = -> Pad017
  Length = 5
  Length2 = 100
  Midplane = true
  Profile = -> Sketch043
  Type = 1
FEATURE [PartDesign::Body] Body011  label="bearing-hub-top"
  Group = -> [Sketch039,Pad016,Sketch040,Pocket022,Sketch041,Pocket023,PolarPattern001,Sketch042,Pad017,Sketch043,Pocket024]
  Origin = -> Origin020
  Tip = -> Pocket024
FEATURE [App::Part] Part007  label="peristaltic_body"
  Group = -> [Body007,Body008,Body009,Body010,Body011]
  Origin = -> Origin014
